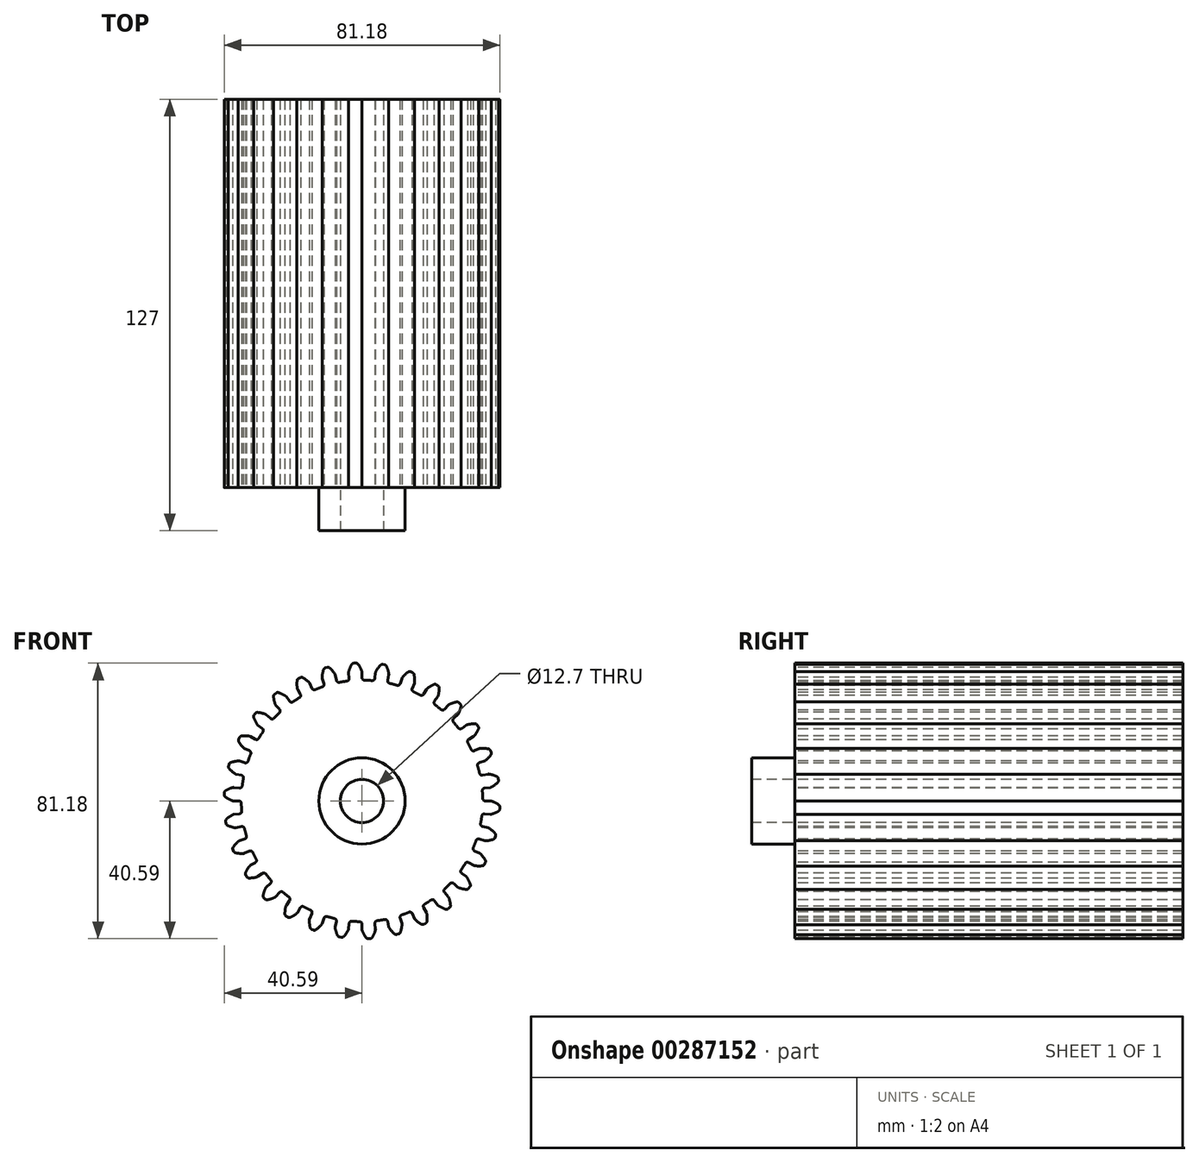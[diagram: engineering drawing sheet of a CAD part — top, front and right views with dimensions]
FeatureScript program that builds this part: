
annotation { "Feature Type Name" : "Feature", "Feature Type Description" : "" }
export const myFeature = defineFeature(function(context is Context, id is Id, definition is map)
    precondition{}
    {
        {
            var Q0;
            Q0=qCreatedBy(makeId("Front.planeOp"),FACE);
            var sketch = newSketch(context, id + "F0", { "sketchPlane" : qUnion([Q0])});
            skCircle(sketch, "E0", {"center": v(0, 0) * mm, "radius": 35.56 * mm});
            skSolve(sketch);
        }
        {
            var Q0;
            Q0=qSketchRegion(id+"F0",true);
            extrude(context, id + "F1", {"entities" : qUnion([Q0]), "depth" : 57.15 * mm});
        }
        {
            var Q0;
            Q0=makeQuery(id+"F1.opExtrude","CAP_FACE",FACE,{"disambiguationData":[OSD([sQuery(id+"F0.wireOp",EDGE,"E0")])],"isStart":true});
            extrude(context, id + "F2", {"entities" : qUnion([Q0]), "operationType" : NewBodyOperationType.ADD, "depth" : 57.15 * mm});
        }
        {
            var Q0;
            Q0=makeQuery(id+"F1.opExtrude","CAP_FACE",FACE,{"disambiguationData":[OSD([sQuery(id+"F0.wireOp",EDGE,"E0")])],"isStart":false});
            var sketch = newSketch(context, id + "F3", { "sketchPlane" : qUnion([Q0])});
            skArc(sketch, "E1.trimOffspring", {"start": v(-0.06, 38.24) * mm, "mid": v(-0.56, 39.3) * mm, "end": v(-1.18, 40.28) * mm});
            skLineSegment(sketch, "E2", {"start": v(-1.84, 40.6) * mm, "end": v(-2.13, 40.58) * mm});
            skLineSegment(sketch, "E3", {"start": v(0, 37.96) * mm, "end": v(0, 36.31) * mm});
            skLineSegment(sketch, "E4.MirrorCS", {"start": v(-2.41, 40.56) * mm, "end": v(-2.13, 40.58) * mm});
            skArc(sketch, "E5.MirrorCS", {"start": v(-3.94, 38.04) * mm, "mid": v(-3.55, 39.14) * mm, "end": v(-3.03, 40.18) * mm});
            skPoint(sketch, "E6.visualSharp", {"position": v(-3.76, 35.36) * mm});
            skPoint(sketch, "E7.visualSharp", {"position": v(0, 35.56) * mm});
            skArc(sketch, "E7.filletArc", {"start": v(0, 36.31) * mm, "mid": v(0.22, 35.78) * mm, "end": v(0.75, 35.55) * mm});
            skArc(sketch, "E8", {"start": v(0.75, 35.55) * mm, "mid": v(-1.88, 35.51) * mm, "end": v(-4.5, 35.27) * mm});
            skLineSegment(sketch, "E9.MirrorCS", {"start": v(-3.97, 37.75) * mm, "end": v(-3.8, 36.12) * mm});
            skArc(sketch, "E10.MirrorCS", {"start": v(-3.8, 36.12) * mm, "mid": v(-3.96, 35.56) * mm, "end": v(-4.46, 35.28) * mm});
            skPoint(sketch, "E11.visualSharp", {"position": v(-3.98, 37.9) * mm});
            skArc(sketch, "E11.filletArc", {"start": v(-3.94, 38.04) * mm, "mid": v(-3.97, 37.9) * mm, "end": v(-3.97, 37.75) * mm});
            skPoint(sketch, "E12.visualSharp", {"position": v(-2.81, 40.54) * mm});
            skArc(sketch, "E12.filletArc", {"start": v(-2.41, 40.56) * mm, "mid": v(-2.77, 40.45) * mm, "end": v(-3.03, 40.18) * mm});
            skPoint(sketch, "E13.visualSharp", {"position": v(-1.44, 40.61) * mm});
            skArc(sketch, "E13.filletArc", {"start": v(-1.18, 40.28) * mm, "mid": v(-1.47, 40.52) * mm, "end": v(-1.84, 40.6) * mm});
            skPoint(sketch, "E14.visualSharp", {"position": v(0, 38.1) * mm});
            skArc(sketch, "E14.filletArc", {"start": v(0, 37.96) * mm, "mid": v(-0.01, 38.1) * mm, "end": v(-0.06, 38.24) * mm});
            skPoint(sketch, "E15.1.0", {"position": v(-11.77, 36.24) * mm});
            skArc(sketch, "E15.1.1", {"start": v(-6.66, 34.93) * mm, "mid": v(-9.22, 34.34) * mm, "end": v(-11.73, 33.57) * mm});
            skLineSegment(sketch, "E15.1.2", {"start": v(-11.73, 36.1) * mm, "end": v(-11.22, 34.54) * mm});
            skArc(sketch, "E15.1.3", {"start": v(-7.55, 35.52) * mm, "mid": v(-7.23, 35.04) * mm, "end": v(-6.66, 34.93) * mm});
            skPoint(sketch, "E15.1.4", {"position": v(-7.92, 37.27) * mm});
            skPoint(sketch, "E15.1.5", {"position": v(-7.4, 34.78) * mm});
            skArc(sketch, "E15.1.6", {"start": v(-11.22, 34.54) * mm, "mid": v(-11.26, 33.96) * mm, "end": v(-11.7, 33.58) * mm});
            skArc(sketch, "E15.1.7", {"start": v(-11.76, 36.39) * mm, "mid": v(-11.61, 37.54) * mm, "end": v(-11.32, 38.68) * mm});
            skPoint(sketch, "E15.1.8", {"position": v(-11.18, 39.07) * mm});
            skArc(sketch, "E15.1.9", {"start": v(-8, 37.4) * mm, "mid": v(-8.72, 38.32) * mm, "end": v(-9.53, 39.15) * mm});
            skPoint(sketch, "E15.1.10", {"position": v(-9.85, 39.43) * mm});
            skPoint(sketch, "E15.1.11", {"position": v(-11.03, 33.8) * mm});
            skLineSegment(sketch, "E15.1.12", {"start": v(-7.9, 37.13) * mm, "end": v(-7.55, 35.52) * mm});
            skArc(sketch, "E15.1.13", {"start": v(-9.53, 39.15) * mm, "mid": v(-9.87, 39.33) * mm, "end": v(-10.24, 39.32) * mm});
            skArc(sketch, "E15.1.14", {"start": v(-10.8, 39.18) * mm, "mid": v(-11.12, 39) * mm, "end": v(-11.32, 38.68) * mm});
            skLineSegment(sketch, "E15.1.15", {"start": v(-10.8, 39.18) * mm, "end": v(-10.52, 39.25) * mm});
            skLineSegment(sketch, "E15.1.16", {"start": v(-10.24, 39.32) * mm, "end": v(-10.52, 39.25) * mm});
            skArc(sketch, "E15.1.17", {"start": v(-11.76, 36.39) * mm, "mid": v(-11.76, 36.24) * mm, "end": v(-11.73, 36.1) * mm});
            skArc(sketch, "E15.1.18", {"start": v(-7.9, 37.13) * mm, "mid": v(-7.94, 37.27) * mm, "end": v(-8, 37.4) * mm});
            skPoint(sketch, "E15.2.0", {"position": v(-19.05, 33) * mm});
            skArc(sketch, "E15.2.1", {"start": v(-13.78, 32.78) * mm, "mid": v(-16.16, 31.67) * mm, "end": v(-18.46, 30.4) * mm});
            skLineSegment(sketch, "E15.2.2", {"start": v(-18.98, 32.87) * mm, "end": v(-18.16, 31.45) * mm});
            skArc(sketch, "E15.2.3", {"start": v(-14.77, 33.17) * mm, "mid": v(-14.35, 32.78) * mm, "end": v(-13.78, 32.78) * mm});
            skPoint(sketch, "E15.2.4", {"position": v(-15.5, 34.8) * mm});
            skPoint(sketch, "E15.2.5", {"position": v(-14.46, 32.49) * mm});
            skArc(sketch, "E15.2.6", {"start": v(-18.16, 31.45) * mm, "mid": v(-18.08, 30.88) * mm, "end": v(-18.42, 30.42) * mm});
            skArc(sketch, "E15.2.7", {"start": v(-19.07, 33.14) * mm, "mid": v(-19.16, 34.3) * mm, "end": v(-19.11, 35.48) * mm});
            skPoint(sketch, "E15.2.8", {"position": v(-19.06, 35.9) * mm});
            skArc(sketch, "E15.2.9", {"start": v(-15.6, 34.91) * mm, "mid": v(-16.5, 35.67) * mm, "end": v(-17.47, 36.32) * mm});
            skPoint(sketch, "E15.2.10", {"position": v(-17.83, 36.52) * mm});
            skPoint(sketch, "E15.2.11", {"position": v(-17.82, 30.77) * mm});
            skLineSegment(sketch, "E15.2.12", {"start": v(-15.44, 34.67) * mm, "end": v(-14.77, 33.17) * mm});
            skArc(sketch, "E15.2.13", {"start": v(-17.47, 36.32) * mm, "mid": v(-17.83, 36.42) * mm, "end": v(-18.2, 36.34) * mm});
            skArc(sketch, "E15.2.14", {"start": v(-18.7, 36.08) * mm, "mid": v(-18.98, 35.83) * mm, "end": v(-19.11, 35.48) * mm});
            skLineSegment(sketch, "E15.2.15", {"start": v(-18.7, 36.08) * mm, "end": v(-18.45, 36.2) * mm});
            skLineSegment(sketch, "E15.2.16", {"start": v(-18.2, 36.34) * mm, "end": v(-18.45, 36.2) * mm});
            skArc(sketch, "E15.2.17", {"start": v(-19.07, 33.14) * mm, "mid": v(-19.04, 33) * mm, "end": v(-18.98, 32.87) * mm});
            skArc(sketch, "E15.2.18", {"start": v(-15.44, 34.67) * mm, "mid": v(-15.5, 34.8) * mm, "end": v(-15.6, 34.91) * mm});
            skArc(sketch, "E16.1.3.0", {"start": v(-20.3, 29.2) * mm, "mid": v(-22.4, 27.62) * mm, "end": v(-24.37, 25.9) * mm});
            skLineSegment(sketch, "E16.5.3.0", {"start": v(-25.4, 28.2) * mm, "end": v(-24.3, 26.99) * mm});
            skArc(sketch, "E16.8.3.0", {"start": v(-21.34, 29.38) * mm, "mid": v(-20.86, 29.08) * mm, "end": v(-20.3, 29.2) * mm});
            skPoint(sketch, "E16.12.3.0", {"position": v(-22.4, 30.82) * mm});
            skPoint(sketch, "E16.13.3.0", {"position": v(-20.9, 28.77) * mm});
            skArc(sketch, "E16.14.3.0", {"start": v(-24.3, 26.99) * mm, "mid": v(-24.1, 26.44) * mm, "end": v(-24.34, 25.92) * mm});
            skArc(sketch, "E16.18.3.0", {"start": v(-25.55, 28.45) * mm, "mid": v(-25.88, 29.57) * mm, "end": v(-26.07, 30.73) * mm});
            skPoint(sketch, "E16.22.3.0", {"position": v(-26.1, 31.15) * mm});
            skArc(sketch, "E16.23.3.0", {"start": v(-22.52, 30.9) * mm, "mid": v(-23.55, 31.46) * mm, "end": v(-24.63, 31.9) * mm});
            skPoint(sketch, "E16.24.3.0", {"position": v(-25.5, 28.31) * mm});
            skPoint(sketch, "E16.27.3.0", {"position": v(-25.04, 32.01) * mm});
            skPoint(sketch, "E16.28.3.0", {"position": v(-23.83, 26.4) * mm});
            skLineSegment(sketch, "E16.29.3.0", {"start": v(-22.3, 30.7) * mm, "end": v(-21.34, 29.38) * mm});
            skArc(sketch, "E16.32.3.0", {"start": v(-24.63, 31.9) * mm, "mid": v(-25, 31.92) * mm, "end": v(-25.35, 31.76) * mm});
            skArc(sketch, "E16.36.3.0", {"start": v(-25.8, 31.4) * mm, "mid": v(-26.02, 31.1) * mm, "end": v(-26.07, 30.73) * mm});
            skLineSegment(sketch, "E16.40.3.0", {"start": v(-25.8, 31.4) * mm, "end": v(-25.57, 31.58) * mm});
            skLineSegment(sketch, "E16.43.3.0", {"start": v(-25.35, 31.76) * mm, "end": v(-25.57, 31.58) * mm});
            skArc(sketch, "E16.46.3.0", {"start": v(-25.55, 28.45) * mm, "mid": v(-25.48, 28.32) * mm, "end": v(-25.4, 28.2) * mm});
            skArc(sketch, "E16.50.3.0", {"start": v(-22.3, 30.7) * mm, "mid": v(-22.4, 30.82) * mm, "end": v(-22.52, 30.9) * mm});
            skArc(sketch, "E16.1.4.0", {"start": v(-25.92, 24.34) * mm, "mid": v(-27.65, 22.36) * mm, "end": v(-29.22, 20.26) * mm});
            skLineSegment(sketch, "E16.5.4.0", {"start": v(-30.7, 22.3) * mm, "end": v(-29.38, 21.34) * mm});
            skArc(sketch, "E16.8.4.0", {"start": v(-26.99, 24.3) * mm, "mid": v(-26.44, 24.1) * mm, "end": v(-25.92, 24.34) * mm});
            skPoint(sketch, "E16.12.4.0", {"position": v(-28.31, 25.5) * mm});
            skPoint(sketch, "E16.13.4.0", {"position": v(-26.43, 23.8) * mm});
            skArc(sketch, "E16.14.4.0", {"start": v(-29.38, 21.34) * mm, "mid": v(-29.08, 20.86) * mm, "end": v(-29.2, 20.3) * mm});
            skArc(sketch, "E16.18.4.0", {"start": v(-30.9, 22.52) * mm, "mid": v(-31.46, 23.55) * mm, "end": v(-31.9, 24.63) * mm});
            skPoint(sketch, "E16.22.4.0", {"position": v(-32.01, 25.04) * mm});
            skArc(sketch, "E16.23.4.0", {"start": v(-28.45, 25.55) * mm, "mid": v(-29.57, 25.88) * mm, "end": v(-30.73, 26.07) * mm});
            skPoint(sketch, "E16.24.4.0", {"position": v(-30.82, 22.4) * mm});
            skPoint(sketch, "E16.27.4.0", {"position": v(-31.15, 26.1) * mm});
            skPoint(sketch, "E16.28.4.0", {"position": v(-28.8, 20.87) * mm});
            skLineSegment(sketch, "E16.29.4.0", {"start": v(-28.2, 25.4) * mm, "end": v(-26.99, 24.3) * mm});
            skArc(sketch, "E16.32.4.0", {"start": v(-30.73, 26.07) * mm, "mid": v(-31.1, 26.02) * mm, "end": v(-31.4, 25.8) * mm});
            skArc(sketch, "E16.36.4.0", {"start": v(-31.76, 25.35) * mm, "mid": v(-31.92, 25) * mm, "end": v(-31.9, 24.63) * mm});
            skLineSegment(sketch, "E16.40.4.0", {"start": v(-31.76, 25.35) * mm, "end": v(-31.58, 25.57) * mm});
            skLineSegment(sketch, "E16.43.4.0", {"start": v(-31.4, 25.8) * mm, "end": v(-31.58, 25.57) * mm});
            skArc(sketch, "E16.46.4.0", {"start": v(-30.9, 22.52) * mm, "mid": v(-30.82, 22.4) * mm, "end": v(-30.7, 22.3) * mm});
            skArc(sketch, "E16.50.4.0", {"start": v(-28.2, 25.4) * mm, "mid": v(-28.32, 25.48) * mm, "end": v(-28.45, 25.55) * mm});
            skArc(sketch, "E16.1.5.0", {"start": v(-30.42, 18.42) * mm, "mid": v(-31.7, 16.13) * mm, "end": v(-32.8, 13.74) * mm});
            skLineSegment(sketch, "E16.5.5.0", {"start": v(-34.67, 15.44) * mm, "end": v(-33.17, 14.77) * mm});
            skArc(sketch, "E16.8.5.0", {"start": v(-31.45, 18.16) * mm, "mid": v(-30.88, 18.08) * mm, "end": v(-30.42, 18.42) * mm});
            skPoint(sketch, "E16.12.5.0", {"position": v(-33, 19.05) * mm});
            skPoint(sketch, "E16.13.5.0", {"position": v(-30.8, 17.78) * mm});
            skArc(sketch, "E16.14.5.0", {"start": v(-33.17, 14.77) * mm, "mid": v(-32.78, 14.35) * mm, "end": v(-32.78, 13.78) * mm});
            skArc(sketch, "E16.18.5.0", {"start": v(-34.91, 15.6) * mm, "mid": v(-35.67, 16.5) * mm, "end": v(-36.32, 17.47) * mm});
            skPoint(sketch, "E16.22.5.0", {"position": v(-36.52, 17.83) * mm});
            skArc(sketch, "E16.23.5.0", {"start": v(-33.14, 19.07) * mm, "mid": v(-34.3, 19.16) * mm, "end": v(-35.48, 19.11) * mm});
            skPoint(sketch, "E16.24.5.0", {"position": v(-34.8, 15.5) * mm});
            skPoint(sketch, "E16.27.5.0", {"position": v(-35.9, 19.06) * mm});
            skPoint(sketch, "E16.28.5.0", {"position": v(-32.5, 14.42) * mm});
            skLineSegment(sketch, "E16.29.5.0", {"start": v(-32.87, 18.98) * mm, "end": v(-31.45, 18.16) * mm});
            skArc(sketch, "E16.32.5.0", {"start": v(-35.48, 19.11) * mm, "mid": v(-35.83, 18.98) * mm, "end": v(-36.08, 18.7) * mm});
            skArc(sketch, "E16.36.5.0", {"start": v(-36.34, 18.2) * mm, "mid": v(-36.42, 17.83) * mm, "end": v(-36.32, 17.47) * mm});
            skLineSegment(sketch, "E16.40.5.0", {"start": v(-36.34, 18.2) * mm, "end": v(-36.2, 18.45) * mm});
            skLineSegment(sketch, "E16.43.5.0", {"start": v(-36.08, 18.7) * mm, "end": v(-36.2, 18.45) * mm});
            skArc(sketch, "E16.46.5.0", {"start": v(-34.91, 15.6) * mm, "mid": v(-34.8, 15.5) * mm, "end": v(-34.67, 15.44) * mm});
            skArc(sketch, "E16.50.5.0", {"start": v(-32.87, 18.98) * mm, "mid": v(-33, 19.04) * mm, "end": v(-33.14, 19.07) * mm});
            skArc(sketch, "E16.1.6.0", {"start": v(-33.58, 11.7) * mm, "mid": v(-34.35, 9.18) * mm, "end": v(-34.94, 6.62) * mm});
            skLineSegment(sketch, "E16.5.6.0", {"start": v(-37.13, 7.9) * mm, "end": v(-35.52, 7.55) * mm});
            skArc(sketch, "E16.8.6.0", {"start": v(-34.54, 11.22) * mm, "mid": v(-33.96, 11.26) * mm, "end": v(-33.58, 11.7) * mm});
            skPoint(sketch, "E16.12.6.0", {"position": v(-36.24, 11.77) * mm});
            skPoint(sketch, "E16.13.6.0", {"position": v(-33.82, 10.99) * mm});
            skArc(sketch, "E16.14.6.0", {"start": v(-35.52, 7.55) * mm, "mid": v(-35.04, 7.23) * mm, "end": v(-34.93, 6.66) * mm});
            skArc(sketch, "E16.18.6.0", {"start": v(-37.4, 8) * mm, "mid": v(-38.32, 8.72) * mm, "end": v(-39.15, 9.53) * mm});
            skPoint(sketch, "E16.22.6.0", {"position": v(-39.43, 9.85) * mm});
            skArc(sketch, "E16.23.6.0", {"start": v(-36.39, 11.76) * mm, "mid": v(-37.54, 11.61) * mm, "end": v(-38.68, 11.32) * mm});
            skPoint(sketch, "E16.24.6.0", {"position": v(-37.27, 7.92) * mm});
            skPoint(sketch, "E16.27.6.0", {"position": v(-39.07, 11.18) * mm});
            skPoint(sketch, "E16.28.6.0", {"position": v(-34.8, 7.35) * mm});
            skLineSegment(sketch, "E16.29.6.0", {"start": v(-36.1, 11.73) * mm, "end": v(-34.54, 11.22) * mm});
            skArc(sketch, "E16.32.6.0", {"start": v(-38.68, 11.32) * mm, "mid": v(-39, 11.12) * mm, "end": v(-39.18, 10.8) * mm});
            skArc(sketch, "E16.36.6.0", {"start": v(-39.32, 10.24) * mm, "mid": v(-39.33, 9.87) * mm, "end": v(-39.15, 9.53) * mm});
            skLineSegment(sketch, "E16.40.6.0", {"start": v(-39.32, 10.24) * mm, "end": v(-39.25, 10.52) * mm});
            skLineSegment(sketch, "E16.43.6.0", {"start": v(-39.18, 10.8) * mm, "end": v(-39.25, 10.52) * mm});
            skArc(sketch, "E16.46.6.0", {"start": v(-37.4, 8) * mm, "mid": v(-37.27, 7.94) * mm, "end": v(-37.13, 7.9) * mm});
            skArc(sketch, "E16.50.6.0", {"start": v(-36.1, 11.73) * mm, "mid": v(-36.24, 11.76) * mm, "end": v(-36.39, 11.76) * mm});
            skArc(sketch, "E16.1.7.0", {"start": v(-35.28, 4.46) * mm, "mid": v(-35.51, 1.84) * mm, "end": v(-35.55, -0.79) * mm});
            skLineSegment(sketch, "E16.5.7.0", {"start": v(-37.96, 0) * mm, "end": v(-36.31, 0) * mm});
            skArc(sketch, "E16.8.7.0", {"start": v(-36.12, 3.8) * mm, "mid": v(-35.56, 3.96) * mm, "end": v(-35.28, 4.46) * mm});
            skPoint(sketch, "E16.12.7.0", {"position": v(-37.9, 3.98) * mm});
            skPoint(sketch, "E16.13.7.0", {"position": v(-35.37, 3.72) * mm});
            skArc(sketch, "E16.14.7.0", {"start": v(-36.31, 0) * mm, "mid": v(-35.78, -0.22) * mm, "end": v(-35.55, -0.75) * mm});
            skArc(sketch, "E16.18.7.0", {"start": v(-38.24, 0.06) * mm, "mid": v(-39.3, 0.56) * mm, "end": v(-40.28, 1.18) * mm});
            skPoint(sketch, "E16.22.7.0", {"position": v(-40.61, 1.44) * mm});
            skArc(sketch, "E16.23.7.0", {"start": v(-38.04, 3.94) * mm, "mid": v(-39.14, 3.55) * mm, "end": v(-40.18, 3.03) * mm});
            skPoint(sketch, "E16.24.7.0", {"position": v(-38.1, 0) * mm});
            skPoint(sketch, "E16.27.7.0", {"position": v(-40.54, 2.81) * mm});
            skPoint(sketch, "E16.28.7.0", {"position": v(-35.56, -0.04) * mm});
            skLineSegment(sketch, "E16.29.7.0", {"start": v(-37.75, 3.97) * mm, "end": v(-36.12, 3.8) * mm});
            skArc(sketch, "E16.32.7.0", {"start": v(-40.18, 3.03) * mm, "mid": v(-40.45, 2.77) * mm, "end": v(-40.56, 2.41) * mm});
            skArc(sketch, "E16.36.7.0", {"start": v(-40.6, 1.84) * mm, "mid": v(-40.52, 1.47) * mm, "end": v(-40.28, 1.18) * mm});
            skLineSegment(sketch, "E16.40.7.0", {"start": v(-40.6, 1.84) * mm, "end": v(-40.58, 2.13) * mm});
            skLineSegment(sketch, "E16.43.7.0", {"start": v(-40.56, 2.41) * mm, "end": v(-40.58, 2.13) * mm});
            skArc(sketch, "E16.46.7.0", {"start": v(-38.24, 0.06) * mm, "mid": v(-38.1, 0.01) * mm, "end": v(-37.96, 0) * mm});
            skArc(sketch, "E16.50.7.0", {"start": v(-37.75, 3.97) * mm, "mid": v(-37.9, 3.97) * mm, "end": v(-38.04, 3.94) * mm});
            skArc(sketch, "E16.1.8.0", {"start": v(-35.44, -2.97) * mm, "mid": v(-35.12, -5.58) * mm, "end": v(-34.61, -8.16) * mm});
            skLineSegment(sketch, "E16.5.8.0", {"start": v(-37.13, -7.9) * mm, "end": v(-35.52, -7.55) * mm});
            skArc(sketch, "E16.8.8.0", {"start": v(-36.12, -3.8) * mm, "mid": v(-35.6, -3.52) * mm, "end": v(-35.44, -2.97) * mm});
            skPoint(sketch, "E16.12.8.0", {"position": v(-37.9, -3.98) * mm});
            skPoint(sketch, "E16.13.8.0", {"position": v(-35.37, -3.72) * mm});
            skArc(sketch, "E16.14.8.0", {"start": v(-35.52, -7.55) * mm, "mid": v(-34.95, -7.65) * mm, "end": v(-34.62, -8.12) * mm});
            skArc(sketch, "E16.18.8.0", {"start": v(-37.42, -7.9) * mm, "mid": v(-38.55, -7.62) * mm, "end": v(-39.65, -7.22) * mm});
            skPoint(sketch, "E16.22.8.0", {"position": v(-40.03, -7.04) * mm});
            skArc(sketch, "E16.23.8.0", {"start": v(-38.02, -4.05) * mm, "mid": v(-39.02, -4.66) * mm, "end": v(-39.94, -5.39) * mm});
            skPoint(sketch, "E16.24.8.0", {"position": v(-37.27, -7.92) * mm});
            skPoint(sketch, "E16.27.8.0", {"position": v(-40.24, -5.68) * mm});
            skPoint(sketch, "E16.28.8.0", {"position": v(-34.77, -7.43) * mm});
            skLineSegment(sketch, "E16.29.8.0", {"start": v(-37.75, -3.97) * mm, "end": v(-36.12, -3.8) * mm});
            skArc(sketch, "E16.32.8.0", {"start": v(-39.94, -5.39) * mm, "mid": v(-40.14, -5.7) * mm, "end": v(-40.18, -6.07) * mm});
            skArc(sketch, "E16.36.8.0", {"start": v(-40.09, -6.64) * mm, "mid": v(-39.94, -6.98) * mm, "end": v(-39.65, -7.22) * mm});
            skLineSegment(sketch, "E16.40.8.0", {"start": v(-40.09, -6.64) * mm, "end": v(-40.13, -6.36) * mm});
            skLineSegment(sketch, "E16.43.8.0", {"start": v(-40.18, -6.07) * mm, "end": v(-40.13, -6.36) * mm});
            skArc(sketch, "E16.46.8.0", {"start": v(-37.42, -7.9) * mm, "mid": v(-37.27, -7.9) * mm, "end": v(-37.13, -7.9) * mm});
            skArc(sketch, "E16.50.8.0", {"start": v(-37.75, -3.97) * mm, "mid": v(-37.9, -4) * mm, "end": v(-38.02, -4.05) * mm});
            skArc(sketch, "E16.1.9.0", {"start": v(-34.04, -10.28) * mm, "mid": v(-33.2, -12.76) * mm, "end": v(-32.16, -15.18) * mm});
            skLineSegment(sketch, "E16.5.9.0", {"start": v(-34.67, -15.44) * mm, "end": v(-33.17, -14.77) * mm});
            skArc(sketch, "E16.8.9.0", {"start": v(-34.54, -11.22) * mm, "mid": v(-34.1, -10.85) * mm, "end": v(-34.04, -10.28) * mm});
            skPoint(sketch, "E16.12.9.0", {"position": v(-36.24, -11.77) * mm});
            skPoint(sketch, "E16.13.9.0", {"position": v(-33.82, -10.99) * mm});
            skArc(sketch, "E16.14.9.0", {"start": v(-33.17, -14.77) * mm, "mid": v(-32.6, -14.75) * mm, "end": v(-32.18, -15.14) * mm});
            skArc(sketch, "E16.18.9.0", {"start": v(-34.96, -15.5) * mm, "mid": v(-36.12, -15.47) * mm, "end": v(-37.28, -15.3) * mm});
            skPoint(sketch, "E16.22.9.0", {"position": v(-37.69, -15.2) * mm});
            skArc(sketch, "E16.23.9.0", {"start": v(-36.35, -11.87) * mm, "mid": v(-37.2, -12.67) * mm, "end": v(-37.94, -13.57) * mm});
            skPoint(sketch, "E16.24.9.0", {"position": v(-34.8, -15.5) * mm});
            skPoint(sketch, "E16.27.9.0", {"position": v(-38.18, -13.92) * mm});
            skPoint(sketch, "E16.28.9.0", {"position": v(-32.47, -14.5) * mm});
            skLineSegment(sketch, "E16.29.9.0", {"start": v(-36.1, -11.73) * mm, "end": v(-34.54, -11.22) * mm});
            skArc(sketch, "E16.32.9.0", {"start": v(-37.94, -13.57) * mm, "mid": v(-38.08, -13.92) * mm, "end": v(-38.04, -14.3) * mm});
            skArc(sketch, "E16.36.9.0", {"start": v(-37.83, -14.83) * mm, "mid": v(-37.62, -15.14) * mm, "end": v(-37.28, -15.3) * mm});
            skLineSegment(sketch, "E16.40.9.0", {"start": v(-37.83, -14.83) * mm, "end": v(-37.94, -14.56) * mm});
            skLineSegment(sketch, "E16.43.9.0", {"start": v(-38.04, -14.3) * mm, "end": v(-37.94, -14.56) * mm});
            skArc(sketch, "E16.46.9.0", {"start": v(-34.96, -15.5) * mm, "mid": v(-34.81, -15.48) * mm, "end": v(-34.67, -15.44) * mm});
            skArc(sketch, "E16.50.9.0", {"start": v(-36.1, -11.73) * mm, "mid": v(-36.23, -11.79) * mm, "end": v(-36.35, -11.87) * mm});
            skArc(sketch, "E16.1.10.0", {"start": v(-31.16, -17.13) * mm, "mid": v(-29.81, -19.38) * mm, "end": v(-28.3, -21.53) * mm});
            skLineSegment(sketch, "E16.5.10.0", {"start": v(-30.7, -22.3) * mm, "end": v(-29.38, -21.34) * mm});
            skArc(sketch, "E16.8.10.0", {"start": v(-31.45, -18.16) * mm, "mid": v(-31.1, -17.7) * mm, "end": v(-31.16, -17.13) * mm});
            skPoint(sketch, "E16.12.10.0", {"position": v(-33, -19.05) * mm});
            skPoint(sketch, "E16.13.10.0", {"position": v(-30.8, -17.78) * mm});
            skArc(sketch, "E16.14.10.0", {"start": v(-29.38, -21.34) * mm, "mid": v(-28.82, -21.2) * mm, "end": v(-28.32, -21.5) * mm});
            skArc(sketch, "E16.18.10.0", {"start": v(-30.97, -22.43) * mm, "mid": v(-32.12, -22.65) * mm, "end": v(-33.28, -22.72) * mm});
            skPoint(sketch, "E16.22.10.0", {"position": v(-33.7, -22.7) * mm});
            skArc(sketch, "E16.23.10.0", {"start": v(-33.09, -19.17) * mm, "mid": v(-33.75, -20.13) * mm, "end": v(-34.3, -21.17) * mm});
            skPoint(sketch, "E16.24.10.0", {"position": v(-30.82, -22.4) * mm});
            skPoint(sketch, "E16.27.10.0", {"position": v(-34.45, -21.55) * mm});
            skPoint(sketch, "E16.28.10.0", {"position": v(-28.74, -20.94) * mm});
            skLineSegment(sketch, "E16.29.10.0", {"start": v(-32.87, -18.98) * mm, "end": v(-31.45, -18.16) * mm});
            skArc(sketch, "E16.32.10.0", {"start": v(-34.3, -21.17) * mm, "mid": v(-34.35, -21.54) * mm, "end": v(-34.23, -21.9) * mm});
            skArc(sketch, "E16.36.10.0", {"start": v(-33.92, -22.37) * mm, "mid": v(-33.65, -22.63) * mm, "end": v(-33.28, -22.72) * mm});
            skLineSegment(sketch, "E16.40.10.0", {"start": v(-33.92, -22.37) * mm, "end": v(-34.08, -22.13) * mm});
            skLineSegment(sketch, "E16.43.10.0", {"start": v(-34.23, -21.9) * mm, "end": v(-34.08, -22.13) * mm});
            skArc(sketch, "E16.46.10.0", {"start": v(-30.97, -22.43) * mm, "mid": v(-30.83, -22.38) * mm, "end": v(-30.7, -22.3) * mm});
            skArc(sketch, "E16.50.10.0", {"start": v(-32.87, -18.98) * mm, "mid": v(-32.99, -19.06) * mm, "end": v(-33.09, -19.17) * mm});
            skArc(sketch, "E16.1.11.0", {"start": v(-26.92, -23.23) * mm, "mid": v(-25.13, -25.16) * mm, "end": v(-23.2, -26.95) * mm});
            skLineSegment(sketch, "E16.5.11.0", {"start": v(-25.4, -28.2) * mm, "end": v(-24.3, -26.99) * mm});
            skArc(sketch, "E16.8.11.0", {"start": v(-26.99, -24.3) * mm, "mid": v(-26.74, -23.78) * mm, "end": v(-26.92, -23.23) * mm});
            skPoint(sketch, "E16.12.11.0", {"position": v(-28.31, -25.5) * mm});
            skPoint(sketch, "E16.13.11.0", {"position": v(-26.43, -23.8) * mm});
            skArc(sketch, "E16.14.11.0", {"start": v(-24.3, -26.99) * mm, "mid": v(-23.78, -26.74) * mm, "end": v(-23.23, -26.92) * mm});
            skArc(sketch, "E16.18.11.0", {"start": v(-25.63, -28.38) * mm, "mid": v(-26.7, -28.83) * mm, "end": v(-27.83, -29.14) * mm});
            skPoint(sketch, "E16.22.11.0", {"position": v(-28.25, -29.22) * mm});
            skArc(sketch, "E16.23.11.0", {"start": v(-28.38, -25.63) * mm, "mid": v(-28.83, -26.7) * mm, "end": v(-29.14, -27.83) * mm});
            skPoint(sketch, "E16.24.11.0", {"position": v(-25.5, -28.31) * mm});
            skPoint(sketch, "E16.27.11.0", {"position": v(-29.22, -28.25) * mm});
            skPoint(sketch, "E16.28.11.0", {"position": v(-23.76, -26.45) * mm});
            skLineSegment(sketch, "E16.29.11.0", {"start": v(-28.2, -25.4) * mm, "end": v(-26.99, -24.3) * mm});
            skArc(sketch, "E16.32.11.0", {"start": v(-29.14, -27.83) * mm, "mid": v(-29.13, -28.2) * mm, "end": v(-28.93, -28.53) * mm});
            skArc(sketch, "E16.36.11.0", {"start": v(-28.53, -28.93) * mm, "mid": v(-28.2, -29.13) * mm, "end": v(-27.83, -29.14) * mm});
            skLineSegment(sketch, "E16.40.11.0", {"start": v(-28.53, -28.93) * mm, "end": v(-28.73, -28.73) * mm});
            skLineSegment(sketch, "E16.43.11.0", {"start": v(-28.93, -28.53) * mm, "end": v(-28.73, -28.73) * mm});
            skArc(sketch, "E16.46.11.0", {"start": v(-25.63, -28.38) * mm, "mid": v(-25.5, -28.3) * mm, "end": v(-25.4, -28.2) * mm});
            skArc(sketch, "E16.50.11.0", {"start": v(-28.2, -25.4) * mm, "mid": v(-28.3, -25.5) * mm, "end": v(-28.38, -25.63) * mm});
            skArc(sketch, "E16.1.12.0", {"start": v(-21.5, -28.32) * mm, "mid": v(-19.35, -29.83) * mm, "end": v(-17.1, -31.18) * mm});
            skLineSegment(sketch, "E16.5.12.0", {"start": v(-18.98, -32.87) * mm, "end": v(-18.16, -31.45) * mm});
            skArc(sketch, "E16.8.12.0", {"start": v(-21.34, -29.38) * mm, "mid": v(-21.2, -28.82) * mm, "end": v(-21.5, -28.32) * mm});
            skPoint(sketch, "E16.12.12.0", {"position": v(-22.4, -30.82) * mm});
            skPoint(sketch, "E16.13.12.0", {"position": v(-20.9, -28.77) * mm});
            skArc(sketch, "E16.14.12.0", {"start": v(-18.16, -31.45) * mm, "mid": v(-17.7, -31.1) * mm, "end": v(-17.13, -31.16) * mm});
            skArc(sketch, "E16.18.12.0", {"start": v(-19.17, -33.09) * mm, "mid": v(-20.13, -33.75) * mm, "end": v(-21.17, -34.3) * mm});
            skPoint(sketch, "E16.22.12.0", {"position": v(-21.55, -34.45) * mm});
            skArc(sketch, "E16.23.12.0", {"start": v(-22.43, -30.97) * mm, "mid": v(-22.65, -32.12) * mm, "end": v(-22.72, -33.28) * mm});
            skPoint(sketch, "E16.24.12.0", {"position": v(-19.05, -33) * mm});
            skPoint(sketch, "E16.27.12.0", {"position": v(-22.7, -33.7) * mm});
            skPoint(sketch, "E16.28.12.0", {"position": v(-17.74, -30.82) * mm});
            skLineSegment(sketch, "E16.29.12.0", {"start": v(-22.3, -30.7) * mm, "end": v(-21.34, -29.38) * mm});
            skArc(sketch, "E16.32.12.0", {"start": v(-22.72, -33.28) * mm, "mid": v(-22.63, -33.65) * mm, "end": v(-22.37, -33.92) * mm});
            skArc(sketch, "E16.36.12.0", {"start": v(-21.9, -34.23) * mm, "mid": v(-21.54, -34.35) * mm, "end": v(-21.17, -34.3) * mm});
            skLineSegment(sketch, "E16.40.12.0", {"start": v(-21.9, -34.23) * mm, "end": v(-22.13, -34.08) * mm});
            skLineSegment(sketch, "E16.43.12.0", {"start": v(-22.37, -33.92) * mm, "end": v(-22.13, -34.08) * mm});
            skArc(sketch, "E16.46.12.0", {"start": v(-19.17, -33.09) * mm, "mid": v(-19.06, -32.99) * mm, "end": v(-18.98, -32.87) * mm});
            skArc(sketch, "E16.50.12.0", {"start": v(-22.3, -30.7) * mm, "mid": v(-22.38, -30.83) * mm, "end": v(-22.43, -30.97) * mm});
            skArc(sketch, "E16.1.13.0", {"start": v(-15.14, -32.18) * mm, "mid": v(-12.72, -33.2) * mm, "end": v(-10.24, -34.05) * mm});
            skLineSegment(sketch, "E16.5.13.0", {"start": v(-11.73, -36.1) * mm, "end": v(-11.22, -34.54) * mm});
            skArc(sketch, "E16.8.13.0", {"start": v(-14.77, -33.17) * mm, "mid": v(-14.75, -32.6) * mm, "end": v(-15.14, -32.18) * mm});
            skPoint(sketch, "E16.12.13.0", {"position": v(-15.5, -34.8) * mm});
            skPoint(sketch, "E16.13.13.0", {"position": v(-14.46, -32.49) * mm});
            skArc(sketch, "E16.14.13.0", {"start": v(-11.22, -34.54) * mm, "mid": v(-10.85, -34.1) * mm, "end": v(-10.28, -34.04) * mm});
            skArc(sketch, "E16.18.13.0", {"start": v(-11.87, -36.35) * mm, "mid": v(-12.67, -37.2) * mm, "end": v(-13.57, -37.94) * mm});
            skPoint(sketch, "E16.22.13.0", {"position": v(-13.92, -38.18) * mm});
            skArc(sketch, "E16.23.13.0", {"start": v(-15.5, -34.96) * mm, "mid": v(-15.47, -36.12) * mm, "end": v(-15.3, -37.28) * mm});
            skPoint(sketch, "E16.24.13.0", {"position": v(-11.77, -36.24) * mm});
            skPoint(sketch, "E16.27.13.0", {"position": v(-15.2, -37.69) * mm});
            skPoint(sketch, "E16.28.13.0", {"position": v(-10.95, -33.83) * mm});
            skLineSegment(sketch, "E16.29.13.0", {"start": v(-15.44, -34.67) * mm, "end": v(-14.77, -33.17) * mm});
            skArc(sketch, "E16.32.13.0", {"start": v(-15.3, -37.28) * mm, "mid": v(-15.14, -37.62) * mm, "end": v(-14.83, -37.83) * mm});
            skArc(sketch, "E16.36.13.0", {"start": v(-14.3, -38.04) * mm, "mid": v(-13.92, -38.08) * mm, "end": v(-13.57, -37.94) * mm});
            skLineSegment(sketch, "E16.40.13.0", {"start": v(-14.3, -38.04) * mm, "end": v(-14.56, -37.94) * mm});
            skLineSegment(sketch, "E16.43.13.0", {"start": v(-14.83, -37.83) * mm, "end": v(-14.56, -37.94) * mm});
            skArc(sketch, "E16.46.13.0", {"start": v(-11.87, -36.35) * mm, "mid": v(-11.79, -36.23) * mm, "end": v(-11.73, -36.1) * mm});
            skArc(sketch, "E16.50.13.0", {"start": v(-15.44, -34.67) * mm, "mid": v(-15.48, -34.81) * mm, "end": v(-15.5, -34.96) * mm});
            skArc(sketch, "E16.1.14.0", {"start": v(-8.12, -34.62) * mm, "mid": v(-5.54, -35.13) * mm, "end": v(-2.93, -35.44) * mm});
            skLineSegment(sketch, "E16.5.14.0", {"start": v(-3.97, -37.75) * mm, "end": v(-3.8, -36.12) * mm});
            skArc(sketch, "E16.8.14.0", {"start": v(-7.55, -35.52) * mm, "mid": v(-7.65, -34.95) * mm, "end": v(-8.12, -34.62) * mm});
            skPoint(sketch, "E16.12.14.0", {"position": v(-7.92, -37.27) * mm});
            skPoint(sketch, "E16.13.14.0", {"position": v(-7.4, -34.78) * mm});
            skArc(sketch, "E16.14.14.0", {"start": v(-3.8, -36.12) * mm, "mid": v(-3.52, -35.6) * mm, "end": v(-2.97, -35.44) * mm});
            skArc(sketch, "E16.18.14.0", {"start": v(-4.05, -38.02) * mm, "mid": v(-4.66, -39.02) * mm, "end": v(-5.39, -39.94) * mm});
            skPoint(sketch, "E16.22.14.0", {"position": v(-5.68, -40.24) * mm});
            skArc(sketch, "E16.23.14.0", {"start": v(-7.9, -37.42) * mm, "mid": v(-7.62, -38.55) * mm, "end": v(-7.22, -39.65) * mm});
            skPoint(sketch, "E16.24.14.0", {"position": v(-3.98, -37.9) * mm});
            skPoint(sketch, "E16.27.14.0", {"position": v(-7.04, -40.03) * mm});
            skPoint(sketch, "E16.28.14.0", {"position": v(-3.67, -35.37) * mm});
            skLineSegment(sketch, "E16.29.14.0", {"start": v(-7.9, -37.13) * mm, "end": v(-7.55, -35.52) * mm});
            skArc(sketch, "E16.32.14.0", {"start": v(-7.22, -39.65) * mm, "mid": v(-6.98, -39.94) * mm, "end": v(-6.64, -40.09) * mm});
            skArc(sketch, "E16.36.14.0", {"start": v(-6.07, -40.18) * mm, "mid": v(-5.7, -40.14) * mm, "end": v(-5.39, -39.94) * mm});
            skLineSegment(sketch, "E16.40.14.0", {"start": v(-6.07, -40.18) * mm, "end": v(-6.36, -40.13) * mm});
            skLineSegment(sketch, "E16.43.14.0", {"start": v(-6.64, -40.09) * mm, "end": v(-6.36, -40.13) * mm});
            skArc(sketch, "E16.46.14.0", {"start": v(-4.05, -38.02) * mm, "mid": v(-4, -37.9) * mm, "end": v(-3.97, -37.75) * mm});
            skArc(sketch, "E16.50.14.0", {"start": v(-7.9, -37.13) * mm, "mid": v(-7.9, -37.27) * mm, "end": v(-7.9, -37.42) * mm});
            skArc(sketch, "E16.1.15.0", {"start": v(-0.75, -35.55) * mm, "mid": v(1.88, -35.51) * mm, "end": v(4.5, -35.27) * mm});
            skLineSegment(sketch, "E16.5.15.0", {"start": v(3.97, -37.75) * mm, "end": v(3.8, -36.12) * mm});
            skArc(sketch, "E16.8.15.0", {"start": v(0, -36.31) * mm, "mid": v(-0.22, -35.78) * mm, "end": v(-0.75, -35.55) * mm});
            skPoint(sketch, "E16.12.15.0", {"position": v(0, -38.1) * mm});
            skPoint(sketch, "E16.13.15.0", {"position": v(0, -35.56) * mm});
            skArc(sketch, "E16.14.15.0", {"start": v(3.8, -36.12) * mm, "mid": v(3.96, -35.56) * mm, "end": v(4.46, -35.28) * mm});
            skArc(sketch, "E16.18.15.0", {"start": v(3.94, -38.04) * mm, "mid": v(3.55, -39.14) * mm, "end": v(3.03, -40.18) * mm});
            skPoint(sketch, "E16.22.15.0", {"position": v(2.81, -40.54) * mm});
            skArc(sketch, "E16.23.15.0", {"start": v(0.06, -38.24) * mm, "mid": v(0.56, -39.3) * mm, "end": v(1.18, -40.28) * mm});
            skPoint(sketch, "E16.24.15.0", {"position": v(3.98, -37.9) * mm});
            skPoint(sketch, "E16.27.15.0", {"position": v(1.44, -40.61) * mm});
            skPoint(sketch, "E16.28.15.0", {"position": v(3.76, -35.36) * mm});
            skLineSegment(sketch, "E16.29.15.0", {"start": v(0, -37.96) * mm, "end": v(0, -36.31) * mm});
            skArc(sketch, "E16.32.15.0", {"start": v(1.18, -40.28) * mm, "mid": v(1.47, -40.52) * mm, "end": v(1.84, -40.6) * mm});
            skArc(sketch, "E16.36.15.0", {"start": v(2.41, -40.56) * mm, "mid": v(2.77, -40.45) * mm, "end": v(3.03, -40.18) * mm});
            skLineSegment(sketch, "E16.40.15.0", {"start": v(2.41, -40.56) * mm, "end": v(2.13, -40.58) * mm});
            skLineSegment(sketch, "E16.43.15.0", {"start": v(1.84, -40.6) * mm, "end": v(2.13, -40.58) * mm});
            skArc(sketch, "E16.46.15.0", {"start": v(3.94, -38.04) * mm, "mid": v(3.97, -37.9) * mm, "end": v(3.97, -37.75) * mm});
            skArc(sketch, "E16.50.15.0", {"start": v(0, -37.96) * mm, "mid": v(0.01, -38.1) * mm, "end": v(0.06, -38.24) * mm});
            skArc(sketch, "E16.1.16.0", {"start": v(6.66, -34.93) * mm, "mid": v(9.22, -34.34) * mm, "end": v(11.73, -33.57) * mm});
            skLineSegment(sketch, "E16.5.16.0", {"start": v(11.73, -36.1) * mm, "end": v(11.22, -34.54) * mm});
            skArc(sketch, "E16.8.16.0", {"start": v(7.55, -35.52) * mm, "mid": v(7.23, -35.04) * mm, "end": v(6.66, -34.93) * mm});
            skPoint(sketch, "E16.12.16.0", {"position": v(7.92, -37.27) * mm});
            skPoint(sketch, "E16.13.16.0", {"position": v(7.4, -34.78) * mm});
            skArc(sketch, "E16.14.16.0", {"start": v(11.22, -34.54) * mm, "mid": v(11.26, -33.96) * mm, "end": v(11.7, -33.58) * mm});
            skArc(sketch, "E16.18.16.0", {"start": v(11.76, -36.39) * mm, "mid": v(11.61, -37.54) * mm, "end": v(11.32, -38.68) * mm});
            skPoint(sketch, "E16.22.16.0", {"position": v(11.18, -39.07) * mm});
            skArc(sketch, "E16.23.16.0", {"start": v(8, -37.4) * mm, "mid": v(8.72, -38.32) * mm, "end": v(9.53, -39.15) * mm});
            skPoint(sketch, "E16.24.16.0", {"position": v(11.77, -36.24) * mm});
            skPoint(sketch, "E16.27.16.0", {"position": v(9.85, -39.43) * mm});
            skPoint(sketch, "E16.28.16.0", {"position": v(11.03, -33.8) * mm});
            skLineSegment(sketch, "E16.29.16.0", {"start": v(7.9, -37.13) * mm, "end": v(7.55, -35.52) * mm});
            skArc(sketch, "E16.32.16.0", {"start": v(9.53, -39.15) * mm, "mid": v(9.87, -39.33) * mm, "end": v(10.24, -39.32) * mm});
            skArc(sketch, "E16.36.16.0", {"start": v(10.8, -39.18) * mm, "mid": v(11.12, -39) * mm, "end": v(11.32, -38.68) * mm});
            skLineSegment(sketch, "E16.40.16.0", {"start": v(10.8, -39.18) * mm, "end": v(10.52, -39.25) * mm});
            skLineSegment(sketch, "E16.43.16.0", {"start": v(10.24, -39.32) * mm, "end": v(10.52, -39.25) * mm});
            skArc(sketch, "E16.46.16.0", {"start": v(11.76, -36.39) * mm, "mid": v(11.76, -36.24) * mm, "end": v(11.73, -36.1) * mm});
            skArc(sketch, "E16.50.16.0", {"start": v(7.9, -37.13) * mm, "mid": v(7.94, -37.27) * mm, "end": v(8, -37.4) * mm});
            skArc(sketch, "E16.1.17.0", {"start": v(13.78, -32.78) * mm, "mid": v(16.16, -31.67) * mm, "end": v(18.46, -30.4) * mm});
            skLineSegment(sketch, "E16.5.17.0", {"start": v(18.98, -32.87) * mm, "end": v(18.16, -31.45) * mm});
            skArc(sketch, "E16.8.17.0", {"start": v(14.77, -33.17) * mm, "mid": v(14.35, -32.78) * mm, "end": v(13.78, -32.78) * mm});
            skPoint(sketch, "E16.12.17.0", {"position": v(15.5, -34.8) * mm});
            skPoint(sketch, "E16.13.17.0", {"position": v(14.46, -32.49) * mm});
            skArc(sketch, "E16.14.17.0", {"start": v(18.16, -31.45) * mm, "mid": v(18.08, -30.88) * mm, "end": v(18.42, -30.42) * mm});
            skArc(sketch, "E16.18.17.0", {"start": v(19.07, -33.14) * mm, "mid": v(19.16, -34.3) * mm, "end": v(19.11, -35.48) * mm});
            skPoint(sketch, "E16.22.17.0", {"position": v(19.06, -35.9) * mm});
            skArc(sketch, "E16.23.17.0", {"start": v(15.6, -34.91) * mm, "mid": v(16.5, -35.67) * mm, "end": v(17.47, -36.32) * mm});
            skPoint(sketch, "E16.24.17.0", {"position": v(19.05, -33) * mm});
            skPoint(sketch, "E16.27.17.0", {"position": v(17.83, -36.52) * mm});
            skPoint(sketch, "E16.28.17.0", {"position": v(17.82, -30.77) * mm});
            skLineSegment(sketch, "E16.29.17.0", {"start": v(15.44, -34.67) * mm, "end": v(14.77, -33.17) * mm});
            skArc(sketch, "E16.32.17.0", {"start": v(17.47, -36.32) * mm, "mid": v(17.83, -36.42) * mm, "end": v(18.2, -36.34) * mm});
            skArc(sketch, "E16.36.17.0", {"start": v(18.7, -36.08) * mm, "mid": v(18.98, -35.83) * mm, "end": v(19.11, -35.48) * mm});
            skLineSegment(sketch, "E16.40.17.0", {"start": v(18.7, -36.08) * mm, "end": v(18.45, -36.2) * mm});
            skLineSegment(sketch, "E16.43.17.0", {"start": v(18.2, -36.34) * mm, "end": v(18.45, -36.2) * mm});
            skArc(sketch, "E16.46.17.0", {"start": v(19.07, -33.14) * mm, "mid": v(19.04, -33) * mm, "end": v(18.98, -32.87) * mm});
            skArc(sketch, "E16.50.17.0", {"start": v(15.44, -34.67) * mm, "mid": v(15.5, -34.8) * mm, "end": v(15.6, -34.91) * mm});
            skArc(sketch, "E16.1.18.0", {"start": v(20.3, -29.2) * mm, "mid": v(22.4, -27.62) * mm, "end": v(24.37, -25.9) * mm});
            skLineSegment(sketch, "E16.5.18.0", {"start": v(25.4, -28.2) * mm, "end": v(24.3, -26.99) * mm});
            skArc(sketch, "E16.8.18.0", {"start": v(21.34, -29.38) * mm, "mid": v(20.86, -29.08) * mm, "end": v(20.3, -29.2) * mm});
            skPoint(sketch, "E16.12.18.0", {"position": v(22.4, -30.82) * mm});
            skPoint(sketch, "E16.13.18.0", {"position": v(20.9, -28.77) * mm});
            skArc(sketch, "E16.14.18.0", {"start": v(24.3, -26.99) * mm, "mid": v(24.1, -26.44) * mm, "end": v(24.34, -25.92) * mm});
            skArc(sketch, "E16.18.18.0", {"start": v(25.55, -28.45) * mm, "mid": v(25.88, -29.57) * mm, "end": v(26.07, -30.73) * mm});
            skPoint(sketch, "E16.22.18.0", {"position": v(26.1, -31.15) * mm});
            skArc(sketch, "E16.23.18.0", {"start": v(22.52, -30.9) * mm, "mid": v(23.55, -31.46) * mm, "end": v(24.63, -31.9) * mm});
            skPoint(sketch, "E16.24.18.0", {"position": v(25.5, -28.31) * mm});
            skPoint(sketch, "E16.27.18.0", {"position": v(25.04, -32.01) * mm});
            skPoint(sketch, "E16.28.18.0", {"position": v(23.83, -26.4) * mm});
            skLineSegment(sketch, "E16.29.18.0", {"start": v(22.3, -30.7) * mm, "end": v(21.34, -29.38) * mm});
            skArc(sketch, "E16.32.18.0", {"start": v(24.63, -31.9) * mm, "mid": v(25, -31.92) * mm, "end": v(25.35, -31.76) * mm});
            skArc(sketch, "E16.36.18.0", {"start": v(25.8, -31.4) * mm, "mid": v(26.02, -31.1) * mm, "end": v(26.07, -30.73) * mm});
            skLineSegment(sketch, "E16.40.18.0", {"start": v(25.8, -31.4) * mm, "end": v(25.57, -31.58) * mm});
            skLineSegment(sketch, "E16.43.18.0", {"start": v(25.35, -31.76) * mm, "end": v(25.57, -31.58) * mm});
            skArc(sketch, "E16.46.18.0", {"start": v(25.55, -28.45) * mm, "mid": v(25.48, -28.32) * mm, "end": v(25.4, -28.2) * mm});
            skArc(sketch, "E16.50.18.0", {"start": v(22.3, -30.7) * mm, "mid": v(22.4, -30.82) * mm, "end": v(22.52, -30.9) * mm});
            skArc(sketch, "E16.1.19.0", {"start": v(25.92, -24.34) * mm, "mid": v(27.65, -22.36) * mm, "end": v(29.22, -20.26) * mm});
            skLineSegment(sketch, "E16.5.19.0", {"start": v(30.7, -22.3) * mm, "end": v(29.38, -21.34) * mm});
            skArc(sketch, "E16.8.19.0", {"start": v(26.99, -24.3) * mm, "mid": v(26.44, -24.1) * mm, "end": v(25.92, -24.34) * mm});
            skPoint(sketch, "E16.12.19.0", {"position": v(28.31, -25.5) * mm});
            skPoint(sketch, "E16.13.19.0", {"position": v(26.43, -23.8) * mm});
            skArc(sketch, "E16.14.19.0", {"start": v(29.38, -21.34) * mm, "mid": v(29.08, -20.86) * mm, "end": v(29.2, -20.3) * mm});
            skArc(sketch, "E16.18.19.0", {"start": v(30.9, -22.52) * mm, "mid": v(31.46, -23.55) * mm, "end": v(31.9, -24.63) * mm});
            skPoint(sketch, "E16.22.19.0", {"position": v(32.01, -25.04) * mm});
            skArc(sketch, "E16.23.19.0", {"start": v(28.45, -25.55) * mm, "mid": v(29.57, -25.88) * mm, "end": v(30.73, -26.07) * mm});
            skPoint(sketch, "E16.24.19.0", {"position": v(30.82, -22.4) * mm});
            skPoint(sketch, "E16.27.19.0", {"position": v(31.15, -26.1) * mm});
            skPoint(sketch, "E16.28.19.0", {"position": v(28.8, -20.87) * mm});
            skLineSegment(sketch, "E16.29.19.0", {"start": v(28.2, -25.4) * mm, "end": v(26.99, -24.3) * mm});
            skArc(sketch, "E16.32.19.0", {"start": v(30.73, -26.07) * mm, "mid": v(31.1, -26.02) * mm, "end": v(31.4, -25.8) * mm});
            skArc(sketch, "E16.36.19.0", {"start": v(31.76, -25.35) * mm, "mid": v(31.92, -25) * mm, "end": v(31.9, -24.63) * mm});
            skLineSegment(sketch, "E16.40.19.0", {"start": v(31.76, -25.35) * mm, "end": v(31.58, -25.57) * mm});
            skLineSegment(sketch, "E16.43.19.0", {"start": v(31.4, -25.8) * mm, "end": v(31.58, -25.57) * mm});
            skArc(sketch, "E16.46.19.0", {"start": v(30.9, -22.52) * mm, "mid": v(30.82, -22.4) * mm, "end": v(30.7, -22.3) * mm});
            skArc(sketch, "E16.50.19.0", {"start": v(28.2, -25.4) * mm, "mid": v(28.32, -25.48) * mm, "end": v(28.45, -25.55) * mm});
            skArc(sketch, "E16.1.20.0", {"start": v(30.42, -18.42) * mm, "mid": v(31.7, -16.13) * mm, "end": v(32.8, -13.74) * mm});
            skLineSegment(sketch, "E16.5.20.0", {"start": v(34.67, -15.44) * mm, "end": v(33.17, -14.77) * mm});
            skArc(sketch, "E16.8.20.0", {"start": v(31.45, -18.16) * mm, "mid": v(30.88, -18.08) * mm, "end": v(30.42, -18.42) * mm});
            skPoint(sketch, "E16.12.20.0", {"position": v(33, -19.05) * mm});
            skPoint(sketch, "E16.13.20.0", {"position": v(30.8, -17.78) * mm});
            skArc(sketch, "E16.14.20.0", {"start": v(33.17, -14.77) * mm, "mid": v(32.78, -14.35) * mm, "end": v(32.78, -13.78) * mm});
            skArc(sketch, "E16.18.20.0", {"start": v(34.91, -15.6) * mm, "mid": v(35.67, -16.5) * mm, "end": v(36.32, -17.47) * mm});
            skPoint(sketch, "E16.22.20.0", {"position": v(36.52, -17.83) * mm});
            skArc(sketch, "E16.23.20.0", {"start": v(33.14, -19.07) * mm, "mid": v(34.3, -19.16) * mm, "end": v(35.48, -19.11) * mm});
            skPoint(sketch, "E16.24.20.0", {"position": v(34.8, -15.5) * mm});
            skPoint(sketch, "E16.27.20.0", {"position": v(35.9, -19.06) * mm});
            skPoint(sketch, "E16.28.20.0", {"position": v(32.5, -14.42) * mm});
            skLineSegment(sketch, "E16.29.20.0", {"start": v(32.87, -18.98) * mm, "end": v(31.45, -18.16) * mm});
            skArc(sketch, "E16.32.20.0", {"start": v(35.48, -19.11) * mm, "mid": v(35.83, -18.98) * mm, "end": v(36.08, -18.7) * mm});
            skArc(sketch, "E16.36.20.0", {"start": v(36.34, -18.2) * mm, "mid": v(36.42, -17.83) * mm, "end": v(36.32, -17.47) * mm});
            skLineSegment(sketch, "E16.40.20.0", {"start": v(36.34, -18.2) * mm, "end": v(36.2, -18.45) * mm});
            skLineSegment(sketch, "E16.43.20.0", {"start": v(36.08, -18.7) * mm, "end": v(36.2, -18.45) * mm});
            skArc(sketch, "E16.46.20.0", {"start": v(34.91, -15.6) * mm, "mid": v(34.8, -15.5) * mm, "end": v(34.67, -15.44) * mm});
            skArc(sketch, "E16.50.20.0", {"start": v(32.87, -18.98) * mm, "mid": v(33, -19.04) * mm, "end": v(33.14, -19.07) * mm});
            skArc(sketch, "E16.1.21.0", {"start": v(33.58, -11.7) * mm, "mid": v(34.35, -9.18) * mm, "end": v(34.94, -6.62) * mm});
            skLineSegment(sketch, "E16.5.21.0", {"start": v(37.13, -7.9) * mm, "end": v(35.52, -7.55) * mm});
            skArc(sketch, "E16.8.21.0", {"start": v(34.54, -11.22) * mm, "mid": v(33.96, -11.26) * mm, "end": v(33.58, -11.7) * mm});
            skPoint(sketch, "E16.12.21.0", {"position": v(36.24, -11.77) * mm});
            skPoint(sketch, "E16.13.21.0", {"position": v(33.82, -10.99) * mm});
            skArc(sketch, "E16.14.21.0", {"start": v(35.52, -7.55) * mm, "mid": v(35.04, -7.23) * mm, "end": v(34.93, -6.66) * mm});
            skArc(sketch, "E16.18.21.0", {"start": v(37.4, -8) * mm, "mid": v(38.32, -8.72) * mm, "end": v(39.15, -9.53) * mm});
            skPoint(sketch, "E16.22.21.0", {"position": v(39.43, -9.85) * mm});
            skArc(sketch, "E16.23.21.0", {"start": v(36.39, -11.76) * mm, "mid": v(37.54, -11.61) * mm, "end": v(38.68, -11.32) * mm});
            skPoint(sketch, "E16.24.21.0", {"position": v(37.27, -7.92) * mm});
            skPoint(sketch, "E16.27.21.0", {"position": v(39.07, -11.18) * mm});
            skPoint(sketch, "E16.28.21.0", {"position": v(34.8, -7.35) * mm});
            skLineSegment(sketch, "E16.29.21.0", {"start": v(36.1, -11.73) * mm, "end": v(34.54, -11.22) * mm});
            skArc(sketch, "E16.32.21.0", {"start": v(38.68, -11.32) * mm, "mid": v(39, -11.12) * mm, "end": v(39.18, -10.8) * mm});
            skArc(sketch, "E16.36.21.0", {"start": v(39.32, -10.24) * mm, "mid": v(39.33, -9.87) * mm, "end": v(39.15, -9.53) * mm});
            skLineSegment(sketch, "E16.40.21.0", {"start": v(39.32, -10.24) * mm, "end": v(39.25, -10.52) * mm});
            skLineSegment(sketch, "E16.43.21.0", {"start": v(39.18, -10.8) * mm, "end": v(39.25, -10.52) * mm});
            skArc(sketch, "E16.46.21.0", {"start": v(37.4, -8) * mm, "mid": v(37.27, -7.94) * mm, "end": v(37.13, -7.9) * mm});
            skArc(sketch, "E16.50.21.0", {"start": v(36.1, -11.73) * mm, "mid": v(36.24, -11.76) * mm, "end": v(36.39, -11.76) * mm});
            skArc(sketch, "E16.1.22.0", {"start": v(35.28, -4.46) * mm, "mid": v(35.51, -1.84) * mm, "end": v(35.55, 0.79) * mm});
            skLineSegment(sketch, "E16.5.22.0", {"start": v(37.96, 0) * mm, "end": v(36.31, 0) * mm});
            skArc(sketch, "E16.8.22.0", {"start": v(36.12, -3.8) * mm, "mid": v(35.56, -3.96) * mm, "end": v(35.28, -4.46) * mm});
            skPoint(sketch, "E16.12.22.0", {"position": v(37.9, -3.98) * mm});
            skPoint(sketch, "E16.13.22.0", {"position": v(35.37, -3.72) * mm});
            skArc(sketch, "E16.14.22.0", {"start": v(36.31, 0) * mm, "mid": v(35.78, 0.22) * mm, "end": v(35.55, 0.75) * mm});
            skArc(sketch, "E16.18.22.0", {"start": v(38.24, -0.06) * mm, "mid": v(39.3, -0.56) * mm, "end": v(40.28, -1.18) * mm});
            skPoint(sketch, "E16.22.22.0", {"position": v(40.61, -1.44) * mm});
            skArc(sketch, "E16.23.22.0", {"start": v(38.04, -3.94) * mm, "mid": v(39.14, -3.55) * mm, "end": v(40.18, -3.03) * mm});
            skPoint(sketch, "E16.24.22.0", {"position": v(38.1, 0) * mm});
            skPoint(sketch, "E16.27.22.0", {"position": v(40.54, -2.81) * mm});
            skPoint(sketch, "E16.28.22.0", {"position": v(35.56, 0.04) * mm});
            skLineSegment(sketch, "E16.29.22.0", {"start": v(37.75, -3.97) * mm, "end": v(36.12, -3.8) * mm});
            skArc(sketch, "E16.32.22.0", {"start": v(40.18, -3.03) * mm, "mid": v(40.45, -2.77) * mm, "end": v(40.56, -2.41) * mm});
            skArc(sketch, "E16.36.22.0", {"start": v(40.6, -1.84) * mm, "mid": v(40.52, -1.47) * mm, "end": v(40.28, -1.18) * mm});
            skLineSegment(sketch, "E16.40.22.0", {"start": v(40.6, -1.84) * mm, "end": v(40.58, -2.13) * mm});
            skLineSegment(sketch, "E16.43.22.0", {"start": v(40.56, -2.41) * mm, "end": v(40.58, -2.13) * mm});
            skArc(sketch, "E16.46.22.0", {"start": v(38.24, -0.06) * mm, "mid": v(38.1, -0.01) * mm, "end": v(37.96, 0) * mm});
            skArc(sketch, "E16.50.22.0", {"start": v(37.75, -3.97) * mm, "mid": v(37.9, -3.97) * mm, "end": v(38.04, -3.94) * mm});
            skArc(sketch, "E16.1.23.0", {"start": v(35.44, 2.97) * mm, "mid": v(35.12, 5.58) * mm, "end": v(34.61, 8.16) * mm});
            skLineSegment(sketch, "E16.5.23.0", {"start": v(37.13, 7.9) * mm, "end": v(35.52, 7.55) * mm});
            skArc(sketch, "E16.8.23.0", {"start": v(36.12, 3.8) * mm, "mid": v(35.6, 3.52) * mm, "end": v(35.44, 2.97) * mm});
            skPoint(sketch, "E16.12.23.0", {"position": v(37.9, 3.98) * mm});
            skPoint(sketch, "E16.13.23.0", {"position": v(35.37, 3.72) * mm});
            skArc(sketch, "E16.14.23.0", {"start": v(35.52, 7.55) * mm, "mid": v(34.95, 7.65) * mm, "end": v(34.62, 8.12) * mm});
            skArc(sketch, "E16.18.23.0", {"start": v(37.42, 7.9) * mm, "mid": v(38.55, 7.62) * mm, "end": v(39.65, 7.22) * mm});
            skPoint(sketch, "E16.22.23.0", {"position": v(40.03, 7.04) * mm});
            skArc(sketch, "E16.23.23.0", {"start": v(38.02, 4.05) * mm, "mid": v(39.02, 4.66) * mm, "end": v(39.94, 5.39) * mm});
            skPoint(sketch, "E16.24.23.0", {"position": v(37.27, 7.92) * mm});
            skPoint(sketch, "E16.27.23.0", {"position": v(40.24, 5.68) * mm});
            skPoint(sketch, "E16.28.23.0", {"position": v(34.77, 7.43) * mm});
            skLineSegment(sketch, "E16.29.23.0", {"start": v(37.75, 3.97) * mm, "end": v(36.12, 3.8) * mm});
            skArc(sketch, "E16.32.23.0", {"start": v(39.94, 5.39) * mm, "mid": v(40.14, 5.7) * mm, "end": v(40.18, 6.07) * mm});
            skArc(sketch, "E16.36.23.0", {"start": v(40.09, 6.64) * mm, "mid": v(39.94, 6.98) * mm, "end": v(39.65, 7.22) * mm});
            skLineSegment(sketch, "E16.40.23.0", {"start": v(40.09, 6.64) * mm, "end": v(40.13, 6.36) * mm});
            skLineSegment(sketch, "E16.43.23.0", {"start": v(40.18, 6.07) * mm, "end": v(40.13, 6.36) * mm});
            skArc(sketch, "E16.46.23.0", {"start": v(37.42, 7.9) * mm, "mid": v(37.27, 7.9) * mm, "end": v(37.13, 7.9) * mm});
            skArc(sketch, "E16.50.23.0", {"start": v(37.75, 3.97) * mm, "mid": v(37.9, 4) * mm, "end": v(38.02, 4.05) * mm});
            skArc(sketch, "E16.1.24.0", {"start": v(34.04, 10.28) * mm, "mid": v(33.2, 12.76) * mm, "end": v(32.16, 15.18) * mm});
            skLineSegment(sketch, "E16.5.24.0", {"start": v(34.67, 15.44) * mm, "end": v(33.17, 14.77) * mm});
            skArc(sketch, "E16.8.24.0", {"start": v(34.54, 11.22) * mm, "mid": v(34.1, 10.85) * mm, "end": v(34.04, 10.28) * mm});
            skPoint(sketch, "E16.12.24.0", {"position": v(36.24, 11.77) * mm});
            skPoint(sketch, "E16.13.24.0", {"position": v(33.82, 10.99) * mm});
            skArc(sketch, "E16.14.24.0", {"start": v(33.17, 14.77) * mm, "mid": v(32.6, 14.75) * mm, "end": v(32.18, 15.14) * mm});
            skArc(sketch, "E16.18.24.0", {"start": v(34.96, 15.5) * mm, "mid": v(36.12, 15.47) * mm, "end": v(37.28, 15.3) * mm});
            skPoint(sketch, "E16.22.24.0", {"position": v(37.69, 15.2) * mm});
            skArc(sketch, "E16.23.24.0", {"start": v(36.35, 11.87) * mm, "mid": v(37.2, 12.67) * mm, "end": v(37.94, 13.57) * mm});
            skPoint(sketch, "E16.24.24.0", {"position": v(34.8, 15.5) * mm});
            skPoint(sketch, "E16.27.24.0", {"position": v(38.18, 13.92) * mm});
            skPoint(sketch, "E16.28.24.0", {"position": v(32.47, 14.5) * mm});
            skLineSegment(sketch, "E16.29.24.0", {"start": v(36.1, 11.73) * mm, "end": v(34.54, 11.22) * mm});
            skArc(sketch, "E16.32.24.0", {"start": v(37.94, 13.57) * mm, "mid": v(38.08, 13.92) * mm, "end": v(38.04, 14.3) * mm});
            skArc(sketch, "E16.36.24.0", {"start": v(37.83, 14.83) * mm, "mid": v(37.62, 15.14) * mm, "end": v(37.28, 15.3) * mm});
            skLineSegment(sketch, "E16.40.24.0", {"start": v(37.83, 14.83) * mm, "end": v(37.94, 14.56) * mm});
            skLineSegment(sketch, "E16.43.24.0", {"start": v(38.04, 14.3) * mm, "end": v(37.94, 14.56) * mm});
            skArc(sketch, "E16.46.24.0", {"start": v(34.96, 15.5) * mm, "mid": v(34.81, 15.48) * mm, "end": v(34.67, 15.44) * mm});
            skArc(sketch, "E16.50.24.0", {"start": v(36.1, 11.73) * mm, "mid": v(36.23, 11.79) * mm, "end": v(36.35, 11.87) * mm});
            skArc(sketch, "E16.1.25.0", {"start": v(31.16, 17.13) * mm, "mid": v(29.81, 19.38) * mm, "end": v(28.3, 21.53) * mm});
            skLineSegment(sketch, "E16.5.25.0", {"start": v(30.7, 22.3) * mm, "end": v(29.38, 21.34) * mm});
            skArc(sketch, "E16.8.25.0", {"start": v(31.45, 18.16) * mm, "mid": v(31.1, 17.7) * mm, "end": v(31.16, 17.13) * mm});
            skPoint(sketch, "E16.12.25.0", {"position": v(33, 19.05) * mm});
            skPoint(sketch, "E16.13.25.0", {"position": v(30.8, 17.78) * mm});
            skArc(sketch, "E16.14.25.0", {"start": v(29.38, 21.34) * mm, "mid": v(28.82, 21.2) * mm, "end": v(28.32, 21.5) * mm});
            skArc(sketch, "E16.18.25.0", {"start": v(30.97, 22.43) * mm, "mid": v(32.12, 22.65) * mm, "end": v(33.28, 22.72) * mm});
            skPoint(sketch, "E16.22.25.0", {"position": v(33.7, 22.7) * mm});
            skArc(sketch, "E16.23.25.0", {"start": v(33.09, 19.17) * mm, "mid": v(33.75, 20.13) * mm, "end": v(34.3, 21.17) * mm});
            skPoint(sketch, "E16.24.25.0", {"position": v(30.82, 22.4) * mm});
            skPoint(sketch, "E16.27.25.0", {"position": v(34.45, 21.55) * mm});
            skPoint(sketch, "E16.28.25.0", {"position": v(28.74, 20.94) * mm});
            skLineSegment(sketch, "E16.29.25.0", {"start": v(32.87, 18.98) * mm, "end": v(31.45, 18.16) * mm});
            skArc(sketch, "E16.32.25.0", {"start": v(34.3, 21.17) * mm, "mid": v(34.35, 21.54) * mm, "end": v(34.23, 21.9) * mm});
            skArc(sketch, "E16.36.25.0", {"start": v(33.92, 22.37) * mm, "mid": v(33.65, 22.63) * mm, "end": v(33.28, 22.72) * mm});
            skLineSegment(sketch, "E16.40.25.0", {"start": v(33.92, 22.37) * mm, "end": v(34.08, 22.13) * mm});
            skLineSegment(sketch, "E16.43.25.0", {"start": v(34.23, 21.9) * mm, "end": v(34.08, 22.13) * mm});
            skArc(sketch, "E16.46.25.0", {"start": v(30.97, 22.43) * mm, "mid": v(30.83, 22.38) * mm, "end": v(30.7, 22.3) * mm});
            skArc(sketch, "E16.50.25.0", {"start": v(32.87, 18.98) * mm, "mid": v(32.99, 19.06) * mm, "end": v(33.09, 19.17) * mm});
            skArc(sketch, "E16.1.26.0", {"start": v(26.92, 23.23) * mm, "mid": v(25.13, 25.16) * mm, "end": v(23.2, 26.95) * mm});
            skLineSegment(sketch, "E16.5.26.0", {"start": v(25.4, 28.2) * mm, "end": v(24.3, 26.99) * mm});
            skArc(sketch, "E16.8.26.0", {"start": v(26.99, 24.3) * mm, "mid": v(26.74, 23.78) * mm, "end": v(26.92, 23.23) * mm});
            skPoint(sketch, "E16.12.26.0", {"position": v(28.31, 25.5) * mm});
            skPoint(sketch, "E16.13.26.0", {"position": v(26.43, 23.8) * mm});
            skArc(sketch, "E16.14.26.0", {"start": v(24.3, 26.99) * mm, "mid": v(23.78, 26.74) * mm, "end": v(23.23, 26.92) * mm});
            skArc(sketch, "E16.18.26.0", {"start": v(25.63, 28.38) * mm, "mid": v(26.7, 28.83) * mm, "end": v(27.83, 29.14) * mm});
            skPoint(sketch, "E16.22.26.0", {"position": v(28.25, 29.22) * mm});
            skArc(sketch, "E16.23.26.0", {"start": v(28.38, 25.63) * mm, "mid": v(28.83, 26.7) * mm, "end": v(29.14, 27.83) * mm});
            skPoint(sketch, "E16.24.26.0", {"position": v(25.5, 28.31) * mm});
            skPoint(sketch, "E16.27.26.0", {"position": v(29.22, 28.25) * mm});
            skPoint(sketch, "E16.28.26.0", {"position": v(23.76, 26.45) * mm});
            skLineSegment(sketch, "E16.29.26.0", {"start": v(28.2, 25.4) * mm, "end": v(26.99, 24.3) * mm});
            skArc(sketch, "E16.32.26.0", {"start": v(29.14, 27.83) * mm, "mid": v(29.13, 28.2) * mm, "end": v(28.93, 28.53) * mm});
            skArc(sketch, "E16.36.26.0", {"start": v(28.53, 28.93) * mm, "mid": v(28.2, 29.13) * mm, "end": v(27.83, 29.14) * mm});
            skLineSegment(sketch, "E16.40.26.0", {"start": v(28.53, 28.93) * mm, "end": v(28.73, 28.73) * mm});
            skLineSegment(sketch, "E16.43.26.0", {"start": v(28.93, 28.53) * mm, "end": v(28.73, 28.73) * mm});
            skArc(sketch, "E16.46.26.0", {"start": v(25.63, 28.38) * mm, "mid": v(25.5, 28.3) * mm, "end": v(25.4, 28.2) * mm});
            skArc(sketch, "E16.50.26.0", {"start": v(28.2, 25.4) * mm, "mid": v(28.3, 25.5) * mm, "end": v(28.38, 25.63) * mm});
            skArc(sketch, "E16.1.27.0", {"start": v(21.5, 28.32) * mm, "mid": v(19.35, 29.83) * mm, "end": v(17.1, 31.18) * mm});
            skLineSegment(sketch, "E16.5.27.0", {"start": v(18.98, 32.87) * mm, "end": v(18.16, 31.45) * mm});
            skArc(sketch, "E16.8.27.0", {"start": v(21.34, 29.38) * mm, "mid": v(21.2, 28.82) * mm, "end": v(21.5, 28.32) * mm});
            skPoint(sketch, "E16.12.27.0", {"position": v(22.4, 30.82) * mm});
            skPoint(sketch, "E16.13.27.0", {"position": v(20.9, 28.77) * mm});
            skArc(sketch, "E16.14.27.0", {"start": v(18.16, 31.45) * mm, "mid": v(17.7, 31.1) * mm, "end": v(17.13, 31.16) * mm});
            skArc(sketch, "E16.18.27.0", {"start": v(19.17, 33.09) * mm, "mid": v(20.13, 33.75) * mm, "end": v(21.17, 34.3) * mm});
            skPoint(sketch, "E16.22.27.0", {"position": v(21.55, 34.45) * mm});
            skArc(sketch, "E16.23.27.0", {"start": v(22.43, 30.97) * mm, "mid": v(22.65, 32.12) * mm, "end": v(22.72, 33.28) * mm});
            skPoint(sketch, "E16.24.27.0", {"position": v(19.05, 33) * mm});
            skPoint(sketch, "E16.27.27.0", {"position": v(22.7, 33.7) * mm});
            skPoint(sketch, "E16.28.27.0", {"position": v(17.74, 30.82) * mm});
            skLineSegment(sketch, "E16.29.27.0", {"start": v(22.3, 30.7) * mm, "end": v(21.34, 29.38) * mm});
            skArc(sketch, "E16.32.27.0", {"start": v(22.72, 33.28) * mm, "mid": v(22.63, 33.65) * mm, "end": v(22.37, 33.92) * mm});
            skArc(sketch, "E16.36.27.0", {"start": v(21.9, 34.23) * mm, "mid": v(21.54, 34.35) * mm, "end": v(21.17, 34.3) * mm});
            skLineSegment(sketch, "E16.40.27.0", {"start": v(21.9, 34.23) * mm, "end": v(22.13, 34.08) * mm});
            skLineSegment(sketch, "E16.43.27.0", {"start": v(22.37, 33.92) * mm, "end": v(22.13, 34.08) * mm});
            skArc(sketch, "E16.46.27.0", {"start": v(19.17, 33.09) * mm, "mid": v(19.06, 32.99) * mm, "end": v(18.98, 32.87) * mm});
            skArc(sketch, "E16.50.27.0", {"start": v(22.3, 30.7) * mm, "mid": v(22.38, 30.83) * mm, "end": v(22.43, 30.97) * mm});
            skArc(sketch, "E16.1.28.0", {"start": v(15.14, 32.18) * mm, "mid": v(12.72, 33.2) * mm, "end": v(10.24, 34.05) * mm});
            skLineSegment(sketch, "E16.5.28.0", {"start": v(11.73, 36.1) * mm, "end": v(11.22, 34.54) * mm});
            skArc(sketch, "E16.8.28.0", {"start": v(14.77, 33.17) * mm, "mid": v(14.75, 32.6) * mm, "end": v(15.14, 32.18) * mm});
            skPoint(sketch, "E16.12.28.0", {"position": v(15.5, 34.8) * mm});
            skPoint(sketch, "E16.13.28.0", {"position": v(14.46, 32.49) * mm});
            skArc(sketch, "E16.14.28.0", {"start": v(11.22, 34.54) * mm, "mid": v(10.85, 34.1) * mm, "end": v(10.28, 34.04) * mm});
            skArc(sketch, "E16.18.28.0", {"start": v(11.87, 36.35) * mm, "mid": v(12.67, 37.2) * mm, "end": v(13.57, 37.94) * mm});
            skPoint(sketch, "E16.22.28.0", {"position": v(13.92, 38.18) * mm});
            skArc(sketch, "E16.23.28.0", {"start": v(15.5, 34.96) * mm, "mid": v(15.47, 36.12) * mm, "end": v(15.3, 37.28) * mm});
            skPoint(sketch, "E16.24.28.0", {"position": v(11.77, 36.24) * mm});
            skPoint(sketch, "E16.27.28.0", {"position": v(15.2, 37.69) * mm});
            skPoint(sketch, "E16.28.28.0", {"position": v(10.95, 33.83) * mm});
            skLineSegment(sketch, "E16.29.28.0", {"start": v(15.44, 34.67) * mm, "end": v(14.77, 33.17) * mm});
            skArc(sketch, "E16.32.28.0", {"start": v(15.3, 37.28) * mm, "mid": v(15.14, 37.62) * mm, "end": v(14.83, 37.83) * mm});
            skArc(sketch, "E16.36.28.0", {"start": v(14.3, 38.04) * mm, "mid": v(13.92, 38.08) * mm, "end": v(13.57, 37.94) * mm});
            skLineSegment(sketch, "E16.40.28.0", {"start": v(14.3, 38.04) * mm, "end": v(14.56, 37.94) * mm});
            skLineSegment(sketch, "E16.43.28.0", {"start": v(14.83, 37.83) * mm, "end": v(14.56, 37.94) * mm});
            skArc(sketch, "E16.46.28.0", {"start": v(11.87, 36.35) * mm, "mid": v(11.79, 36.23) * mm, "end": v(11.73, 36.1) * mm});
            skArc(sketch, "E16.50.28.0", {"start": v(15.44, 34.67) * mm, "mid": v(15.48, 34.81) * mm, "end": v(15.5, 34.96) * mm});
            skArc(sketch, "E16.1.29.0", {"start": v(8.12, 34.62) * mm, "mid": v(5.54, 35.13) * mm, "end": v(2.93, 35.44) * mm});
            skLineSegment(sketch, "E16.5.29.0", {"start": v(3.97, 37.75) * mm, "end": v(3.8, 36.12) * mm});
            skArc(sketch, "E16.8.29.0", {"start": v(7.55, 35.52) * mm, "mid": v(7.65, 34.95) * mm, "end": v(8.12, 34.62) * mm});
            skPoint(sketch, "E16.12.29.0", {"position": v(7.92, 37.27) * mm});
            skPoint(sketch, "E16.13.29.0", {"position": v(7.4, 34.78) * mm});
            skArc(sketch, "E16.14.29.0", {"start": v(3.8, 36.12) * mm, "mid": v(3.52, 35.6) * mm, "end": v(2.97, 35.44) * mm});
            skArc(sketch, "E16.18.29.0", {"start": v(4.05, 38.02) * mm, "mid": v(4.66, 39.02) * mm, "end": v(5.39, 39.94) * mm});
            skPoint(sketch, "E16.22.29.0", {"position": v(5.68, 40.24) * mm});
            skArc(sketch, "E16.23.29.0", {"start": v(7.9, 37.42) * mm, "mid": v(7.62, 38.55) * mm, "end": v(7.22, 39.65) * mm});
            skPoint(sketch, "E16.24.29.0", {"position": v(3.98, 37.9) * mm});
            skPoint(sketch, "E16.27.29.0", {"position": v(7.04, 40.03) * mm});
            skPoint(sketch, "E16.28.29.0", {"position": v(3.67, 35.37) * mm});
            skLineSegment(sketch, "E16.29.29.0", {"start": v(7.9, 37.13) * mm, "end": v(7.55, 35.52) * mm});
            skArc(sketch, "E16.32.29.0", {"start": v(7.22, 39.65) * mm, "mid": v(6.98, 39.94) * mm, "end": v(6.64, 40.09) * mm});
            skArc(sketch, "E16.36.29.0", {"start": v(6.07, 40.18) * mm, "mid": v(5.7, 40.14) * mm, "end": v(5.39, 39.94) * mm});
            skLineSegment(sketch, "E16.40.29.0", {"start": v(6.07, 40.18) * mm, "end": v(6.36, 40.13) * mm});
            skLineSegment(sketch, "E16.43.29.0", {"start": v(6.64, 40.09) * mm, "end": v(6.36, 40.13) * mm});
            skArc(sketch, "E16.46.29.0", {"start": v(4.05, 38.02) * mm, "mid": v(4, 37.9) * mm, "end": v(3.97, 37.75) * mm});
            skArc(sketch, "E16.50.29.0", {"start": v(7.9, 37.13) * mm, "mid": v(7.9, 37.27) * mm, "end": v(7.9, 37.42) * mm});
            skSolve(sketch);
        }
        {
            var Q0;
            Q0=qSketchRegion(id+"F3",true);
            extrude(context, id + "F4", {"entities" : qUnion([Q0]), "operationType" : NewBodyOperationType.ADD, "oppositeDirection" : true, "depth" : 57.15 * mm});
        }
        {
            var Q0;
            Q0=makeQuery(id+"F4.opExtrude","CAP_FACE",FACE,{"disambiguationData":[OSD([sQuery(id+"F3.wireOp",EDGE,"E1.trimOffspring"),sQuery(id+"F3.wireOp",EDGE,"E2"),sQuery(id+"F3.wireOp",EDGE,"E3"),sQuery(id+"F3.wireOp",EDGE,"E4.MirrorCS"),sQuery(id+"F3.wireOp",EDGE,"E5.MirrorCS"),sQuery(id+"F3.wireOp",EDGE,"E7.filletArc"),sQuery(id+"F3.wireOp",EDGE,"E8"),sQuery(id+"F3.wireOp",EDGE,"E9.MirrorCS"),sQuery(id+"F3.wireOp",EDGE,"E10.MirrorCS"),sQuery(id+"F3.wireOp",EDGE,"E11.filletArc"),sQuery(id+"F3.wireOp",EDGE,"E12.filletArc"),sQuery(id+"F3.wireOp",EDGE,"E13.filletArc"),sQuery(id+"F3.wireOp",EDGE,"E14.filletArc")])],"isStart":false});
            var Q1;
            Q1=makeQuery(id+"F4.opExtrude","CAP_FACE",FACE,{"disambiguationData":[OSD([sQuery(id+"F3.wireOp",EDGE,"E15.1.1"),sQuery(id+"F3.wireOp",EDGE,"E15.1.2"),sQuery(id+"F3.wireOp",EDGE,"E15.1.3"),sQuery(id+"F3.wireOp",EDGE,"E15.1.6"),sQuery(id+"F3.wireOp",EDGE,"E15.1.7"),sQuery(id+"F3.wireOp",EDGE,"E15.1.9"),sQuery(id+"F3.wireOp",EDGE,"E15.1.12"),sQuery(id+"F3.wireOp",EDGE,"E15.1.13"),sQuery(id+"F3.wireOp",EDGE,"E15.1.14"),sQuery(id+"F3.wireOp",EDGE,"E15.1.15"),sQuery(id+"F3.wireOp",EDGE,"E15.1.16"),sQuery(id+"F3.wireOp",EDGE,"E15.1.17"),sQuery(id+"F3.wireOp",EDGE,"E15.1.18")])],"isStart":false});
            var Q2;
            Q2=makeQuery(id+"F4.opExtrude","CAP_FACE",FACE,{"disambiguationData":[OSD([sQuery(id+"F3.wireOp",EDGE,"E16.1.29.0"),sQuery(id+"F3.wireOp",EDGE,"E16.5.29.0"),sQuery(id+"F3.wireOp",EDGE,"E16.8.29.0"),sQuery(id+"F3.wireOp",EDGE,"E16.14.29.0"),sQuery(id+"F3.wireOp",EDGE,"E16.18.29.0"),sQuery(id+"F3.wireOp",EDGE,"E16.23.29.0"),sQuery(id+"F3.wireOp",EDGE,"E16.29.29.0"),sQuery(id+"F3.wireOp",EDGE,"E16.32.29.0"),sQuery(id+"F3.wireOp",EDGE,"E16.36.29.0"),sQuery(id+"F3.wireOp",EDGE,"E16.40.29.0"),sQuery(id+"F3.wireOp",EDGE,"E16.43.29.0"),sQuery(id+"F3.wireOp",EDGE,"E16.46.29.0"),sQuery(id+"F3.wireOp",EDGE,"E16.50.29.0")])],"isStart":false});
            var Q3;
            Q3=makeQuery(id+"F4.opExtrude","CAP_FACE",FACE,{"disambiguationData":[OSD([sQuery(id+"F3.wireOp",EDGE,"E16.1.28.0"),sQuery(id+"F3.wireOp",EDGE,"E16.5.28.0"),sQuery(id+"F3.wireOp",EDGE,"E16.8.28.0"),sQuery(id+"F3.wireOp",EDGE,"E16.14.28.0"),sQuery(id+"F3.wireOp",EDGE,"E16.18.28.0"),sQuery(id+"F3.wireOp",EDGE,"E16.23.28.0"),sQuery(id+"F3.wireOp",EDGE,"E16.29.28.0"),sQuery(id+"F3.wireOp",EDGE,"E16.32.28.0"),sQuery(id+"F3.wireOp",EDGE,"E16.36.28.0"),sQuery(id+"F3.wireOp",EDGE,"E16.40.28.0"),sQuery(id+"F3.wireOp",EDGE,"E16.43.28.0"),sQuery(id+"F3.wireOp",EDGE,"E16.46.28.0"),sQuery(id+"F3.wireOp",EDGE,"E16.50.28.0")])],"isStart":false});
            var Q4;
            Q4=makeQuery(id+"F4.opExtrude","CAP_FACE",FACE,{"disambiguationData":[OSD([sQuery(id+"F3.wireOp",EDGE,"E16.1.27.0"),sQuery(id+"F3.wireOp",EDGE,"E16.5.27.0"),sQuery(id+"F3.wireOp",EDGE,"E16.8.27.0"),sQuery(id+"F3.wireOp",EDGE,"E16.14.27.0"),sQuery(id+"F3.wireOp",EDGE,"E16.18.27.0"),sQuery(id+"F3.wireOp",EDGE,"E16.23.27.0"),sQuery(id+"F3.wireOp",EDGE,"E16.29.27.0"),sQuery(id+"F3.wireOp",EDGE,"E16.32.27.0"),sQuery(id+"F3.wireOp",EDGE,"E16.36.27.0"),sQuery(id+"F3.wireOp",EDGE,"E16.40.27.0"),sQuery(id+"F3.wireOp",EDGE,"E16.43.27.0"),sQuery(id+"F3.wireOp",EDGE,"E16.46.27.0"),sQuery(id+"F3.wireOp",EDGE,"E16.50.27.0")])],"isStart":false});
            var Q5;
            Q5=makeQuery(id+"F4.opExtrude","CAP_FACE",FACE,{"disambiguationData":[OSD([sQuery(id+"F3.wireOp",EDGE,"E16.1.26.0"),sQuery(id+"F3.wireOp",EDGE,"E16.5.26.0"),sQuery(id+"F3.wireOp",EDGE,"E16.8.26.0"),sQuery(id+"F3.wireOp",EDGE,"E16.14.26.0"),sQuery(id+"F3.wireOp",EDGE,"E16.18.26.0"),sQuery(id+"F3.wireOp",EDGE,"E16.23.26.0"),sQuery(id+"F3.wireOp",EDGE,"E16.29.26.0"),sQuery(id+"F3.wireOp",EDGE,"E16.32.26.0"),sQuery(id+"F3.wireOp",EDGE,"E16.36.26.0"),sQuery(id+"F3.wireOp",EDGE,"E16.40.26.0"),sQuery(id+"F3.wireOp",EDGE,"E16.43.26.0"),sQuery(id+"F3.wireOp",EDGE,"E16.46.26.0"),sQuery(id+"F3.wireOp",EDGE,"E16.50.26.0")])],"isStart":false});
            var Q6;
            Q6=makeQuery(id+"F4.opExtrude","CAP_FACE",FACE,{"disambiguationData":[OSD([sQuery(id+"F3.wireOp",EDGE,"E16.1.25.0"),sQuery(id+"F3.wireOp",EDGE,"E16.5.25.0"),sQuery(id+"F3.wireOp",EDGE,"E16.8.25.0"),sQuery(id+"F3.wireOp",EDGE,"E16.14.25.0"),sQuery(id+"F3.wireOp",EDGE,"E16.18.25.0"),sQuery(id+"F3.wireOp",EDGE,"E16.23.25.0"),sQuery(id+"F3.wireOp",EDGE,"E16.29.25.0"),sQuery(id+"F3.wireOp",EDGE,"E16.32.25.0"),sQuery(id+"F3.wireOp",EDGE,"E16.36.25.0"),sQuery(id+"F3.wireOp",EDGE,"E16.40.25.0"),sQuery(id+"F3.wireOp",EDGE,"E16.43.25.0"),sQuery(id+"F3.wireOp",EDGE,"E16.46.25.0"),sQuery(id+"F3.wireOp",EDGE,"E16.50.25.0")])],"isStart":false});
            var Q7;
            Q7=makeQuery(id+"F4.opExtrude","CAP_FACE",FACE,{"disambiguationData":[OSD([sQuery(id+"F3.wireOp",EDGE,"E15.2.1"),sQuery(id+"F3.wireOp",EDGE,"E15.2.2"),sQuery(id+"F3.wireOp",EDGE,"E15.2.3"),sQuery(id+"F3.wireOp",EDGE,"E15.2.6"),sQuery(id+"F3.wireOp",EDGE,"E15.2.7"),sQuery(id+"F3.wireOp",EDGE,"E15.2.9"),sQuery(id+"F3.wireOp",EDGE,"E15.2.12"),sQuery(id+"F3.wireOp",EDGE,"E15.2.13"),sQuery(id+"F3.wireOp",EDGE,"E15.2.14"),sQuery(id+"F3.wireOp",EDGE,"E15.2.15"),sQuery(id+"F3.wireOp",EDGE,"E15.2.16"),sQuery(id+"F3.wireOp",EDGE,"E15.2.17"),sQuery(id+"F3.wireOp",EDGE,"E15.2.18")])],"isStart":false});
            var Q8;
            Q8=makeQuery(id+"F4.opExtrude","CAP_FACE",FACE,{"disambiguationData":[OSD([sQuery(id+"F3.wireOp",EDGE,"E16.1.3.0"),sQuery(id+"F3.wireOp",EDGE,"E16.5.3.0"),sQuery(id+"F3.wireOp",EDGE,"E16.8.3.0"),sQuery(id+"F3.wireOp",EDGE,"E16.14.3.0"),sQuery(id+"F3.wireOp",EDGE,"E16.18.3.0"),sQuery(id+"F3.wireOp",EDGE,"E16.23.3.0"),sQuery(id+"F3.wireOp",EDGE,"E16.29.3.0"),sQuery(id+"F3.wireOp",EDGE,"E16.32.3.0"),sQuery(id+"F3.wireOp",EDGE,"E16.36.3.0"),sQuery(id+"F3.wireOp",EDGE,"E16.40.3.0"),sQuery(id+"F3.wireOp",EDGE,"E16.43.3.0"),sQuery(id+"F3.wireOp",EDGE,"E16.46.3.0"),sQuery(id+"F3.wireOp",EDGE,"E16.50.3.0")])],"isStart":false});
            var Q9;
            Q9=makeQuery(id+"F4.opExtrude","CAP_FACE",FACE,{"disambiguationData":[OSD([sQuery(id+"F3.wireOp",EDGE,"E16.1.4.0"),sQuery(id+"F3.wireOp",EDGE,"E16.5.4.0"),sQuery(id+"F3.wireOp",EDGE,"E16.8.4.0"),sQuery(id+"F3.wireOp",EDGE,"E16.14.4.0"),sQuery(id+"F3.wireOp",EDGE,"E16.18.4.0"),sQuery(id+"F3.wireOp",EDGE,"E16.23.4.0"),sQuery(id+"F3.wireOp",EDGE,"E16.29.4.0"),sQuery(id+"F3.wireOp",EDGE,"E16.32.4.0"),sQuery(id+"F3.wireOp",EDGE,"E16.36.4.0"),sQuery(id+"F3.wireOp",EDGE,"E16.40.4.0"),sQuery(id+"F3.wireOp",EDGE,"E16.43.4.0"),sQuery(id+"F3.wireOp",EDGE,"E16.46.4.0"),sQuery(id+"F3.wireOp",EDGE,"E16.50.4.0")])],"isStart":false});
            var Q10;
            Q10=makeQuery(id+"F4.opExtrude","CAP_FACE",FACE,{"disambiguationData":[OSD([sQuery(id+"F3.wireOp",EDGE,"E16.1.5.0"),sQuery(id+"F3.wireOp",EDGE,"E16.5.5.0"),sQuery(id+"F3.wireOp",EDGE,"E16.8.5.0"),sQuery(id+"F3.wireOp",EDGE,"E16.14.5.0"),sQuery(id+"F3.wireOp",EDGE,"E16.18.5.0"),sQuery(id+"F3.wireOp",EDGE,"E16.23.5.0"),sQuery(id+"F3.wireOp",EDGE,"E16.29.5.0"),sQuery(id+"F3.wireOp",EDGE,"E16.32.5.0"),sQuery(id+"F3.wireOp",EDGE,"E16.36.5.0"),sQuery(id+"F3.wireOp",EDGE,"E16.40.5.0"),sQuery(id+"F3.wireOp",EDGE,"E16.43.5.0"),sQuery(id+"F3.wireOp",EDGE,"E16.46.5.0"),sQuery(id+"F3.wireOp",EDGE,"E16.50.5.0")])],"isStart":false});
            var Q11;
            Q11=makeQuery(id+"F4.opExtrude","CAP_FACE",FACE,{"disambiguationData":[OSD([sQuery(id+"F3.wireOp",EDGE,"E16.1.7.0"),sQuery(id+"F3.wireOp",EDGE,"E16.5.7.0"),sQuery(id+"F3.wireOp",EDGE,"E16.8.7.0"),sQuery(id+"F3.wireOp",EDGE,"E16.14.7.0"),sQuery(id+"F3.wireOp",EDGE,"E16.18.7.0"),sQuery(id+"F3.wireOp",EDGE,"E16.23.7.0"),sQuery(id+"F3.wireOp",EDGE,"E16.29.7.0"),sQuery(id+"F3.wireOp",EDGE,"E16.32.7.0"),sQuery(id+"F3.wireOp",EDGE,"E16.36.7.0"),sQuery(id+"F3.wireOp",EDGE,"E16.40.7.0"),sQuery(id+"F3.wireOp",EDGE,"E16.43.7.0"),sQuery(id+"F3.wireOp",EDGE,"E16.46.7.0"),sQuery(id+"F3.wireOp",EDGE,"E16.50.7.0")])],"isStart":false});
            var Q12;
            Q12=makeQuery(id+"F4.opExtrude","CAP_FACE",FACE,{"disambiguationData":[OSD([sQuery(id+"F3.wireOp",EDGE,"E16.1.6.0"),sQuery(id+"F3.wireOp",EDGE,"E16.5.6.0"),sQuery(id+"F3.wireOp",EDGE,"E16.8.6.0"),sQuery(id+"F3.wireOp",EDGE,"E16.14.6.0"),sQuery(id+"F3.wireOp",EDGE,"E16.18.6.0"),sQuery(id+"F3.wireOp",EDGE,"E16.23.6.0"),sQuery(id+"F3.wireOp",EDGE,"E16.29.6.0"),sQuery(id+"F3.wireOp",EDGE,"E16.32.6.0"),sQuery(id+"F3.wireOp",EDGE,"E16.36.6.0"),sQuery(id+"F3.wireOp",EDGE,"E16.40.6.0"),sQuery(id+"F3.wireOp",EDGE,"E16.43.6.0"),sQuery(id+"F3.wireOp",EDGE,"E16.46.6.0"),sQuery(id+"F3.wireOp",EDGE,"E16.50.6.0")])],"isStart":false});
            var Q13;
            Q13=makeQuery(id+"F4.opExtrude","CAP_FACE",FACE,{"disambiguationData":[OSD([sQuery(id+"F3.wireOp",EDGE,"E16.1.9.0"),sQuery(id+"F3.wireOp",EDGE,"E16.5.9.0"),sQuery(id+"F3.wireOp",EDGE,"E16.8.9.0"),sQuery(id+"F3.wireOp",EDGE,"E16.14.9.0"),sQuery(id+"F3.wireOp",EDGE,"E16.18.9.0"),sQuery(id+"F3.wireOp",EDGE,"E16.23.9.0"),sQuery(id+"F3.wireOp",EDGE,"E16.29.9.0"),sQuery(id+"F3.wireOp",EDGE,"E16.32.9.0"),sQuery(id+"F3.wireOp",EDGE,"E16.36.9.0"),sQuery(id+"F3.wireOp",EDGE,"E16.40.9.0"),sQuery(id+"F3.wireOp",EDGE,"E16.43.9.0"),sQuery(id+"F3.wireOp",EDGE,"E16.46.9.0"),sQuery(id+"F3.wireOp",EDGE,"E16.50.9.0")])],"isStart":false});
            var Q14;
            Q14=makeQuery(id+"F4.opExtrude","CAP_FACE",FACE,{"disambiguationData":[OSD([sQuery(id+"F3.wireOp",EDGE,"E16.1.8.0"),sQuery(id+"F3.wireOp",EDGE,"E16.5.8.0"),sQuery(id+"F3.wireOp",EDGE,"E16.8.8.0"),sQuery(id+"F3.wireOp",EDGE,"E16.14.8.0"),sQuery(id+"F3.wireOp",EDGE,"E16.18.8.0"),sQuery(id+"F3.wireOp",EDGE,"E16.23.8.0"),sQuery(id+"F3.wireOp",EDGE,"E16.29.8.0"),sQuery(id+"F3.wireOp",EDGE,"E16.32.8.0"),sQuery(id+"F3.wireOp",EDGE,"E16.36.8.0"),sQuery(id+"F3.wireOp",EDGE,"E16.40.8.0"),sQuery(id+"F3.wireOp",EDGE,"E16.43.8.0"),sQuery(id+"F3.wireOp",EDGE,"E16.46.8.0"),sQuery(id+"F3.wireOp",EDGE,"E16.50.8.0")])],"isStart":false});
            var Q15;
            Q15=makeQuery(id+"F4.opExtrude","CAP_FACE",FACE,{"disambiguationData":[OSD([sQuery(id+"F3.wireOp",EDGE,"E16.1.10.0"),sQuery(id+"F3.wireOp",EDGE,"E16.5.10.0"),sQuery(id+"F3.wireOp",EDGE,"E16.8.10.0"),sQuery(id+"F3.wireOp",EDGE,"E16.14.10.0"),sQuery(id+"F3.wireOp",EDGE,"E16.18.10.0"),sQuery(id+"F3.wireOp",EDGE,"E16.23.10.0"),sQuery(id+"F3.wireOp",EDGE,"E16.29.10.0"),sQuery(id+"F3.wireOp",EDGE,"E16.32.10.0"),sQuery(id+"F3.wireOp",EDGE,"E16.36.10.0"),sQuery(id+"F3.wireOp",EDGE,"E16.40.10.0"),sQuery(id+"F3.wireOp",EDGE,"E16.43.10.0"),sQuery(id+"F3.wireOp",EDGE,"E16.46.10.0"),sQuery(id+"F3.wireOp",EDGE,"E16.50.10.0")])],"isStart":false});
            var Q16;
            Q16=makeQuery(id+"F4.opExtrude","CAP_FACE",FACE,{"disambiguationData":[OSD([sQuery(id+"F3.wireOp",EDGE,"E16.1.11.0"),sQuery(id+"F3.wireOp",EDGE,"E16.5.11.0"),sQuery(id+"F3.wireOp",EDGE,"E16.8.11.0"),sQuery(id+"F3.wireOp",EDGE,"E16.14.11.0"),sQuery(id+"F3.wireOp",EDGE,"E16.18.11.0"),sQuery(id+"F3.wireOp",EDGE,"E16.23.11.0"),sQuery(id+"F3.wireOp",EDGE,"E16.29.11.0"),sQuery(id+"F3.wireOp",EDGE,"E16.32.11.0"),sQuery(id+"F3.wireOp",EDGE,"E16.36.11.0"),sQuery(id+"F3.wireOp",EDGE,"E16.40.11.0"),sQuery(id+"F3.wireOp",EDGE,"E16.43.11.0"),sQuery(id+"F3.wireOp",EDGE,"E16.46.11.0"),sQuery(id+"F3.wireOp",EDGE,"E16.50.11.0")])],"isStart":false});
            var Q17;
            Q17=makeQuery(id+"F4.opExtrude","CAP_FACE",FACE,{"disambiguationData":[OSD([sQuery(id+"F3.wireOp",EDGE,"E16.1.12.0"),sQuery(id+"F3.wireOp",EDGE,"E16.5.12.0"),sQuery(id+"F3.wireOp",EDGE,"E16.8.12.0"),sQuery(id+"F3.wireOp",EDGE,"E16.14.12.0"),sQuery(id+"F3.wireOp",EDGE,"E16.18.12.0"),sQuery(id+"F3.wireOp",EDGE,"E16.23.12.0"),sQuery(id+"F3.wireOp",EDGE,"E16.29.12.0"),sQuery(id+"F3.wireOp",EDGE,"E16.32.12.0"),sQuery(id+"F3.wireOp",EDGE,"E16.36.12.0"),sQuery(id+"F3.wireOp",EDGE,"E16.40.12.0"),sQuery(id+"F3.wireOp",EDGE,"E16.43.12.0"),sQuery(id+"F3.wireOp",EDGE,"E16.46.12.0"),sQuery(id+"F3.wireOp",EDGE,"E16.50.12.0")])],"isStart":false});
            var Q18;
            Q18=makeQuery(id+"F4.opExtrude","CAP_FACE",FACE,{"disambiguationData":[OSD([sQuery(id+"F3.wireOp",EDGE,"E16.1.15.0"),sQuery(id+"F3.wireOp",EDGE,"E16.5.15.0"),sQuery(id+"F3.wireOp",EDGE,"E16.8.15.0"),sQuery(id+"F3.wireOp",EDGE,"E16.14.15.0"),sQuery(id+"F3.wireOp",EDGE,"E16.18.15.0"),sQuery(id+"F3.wireOp",EDGE,"E16.23.15.0"),sQuery(id+"F3.wireOp",EDGE,"E16.29.15.0"),sQuery(id+"F3.wireOp",EDGE,"E16.32.15.0"),sQuery(id+"F3.wireOp",EDGE,"E16.36.15.0"),sQuery(id+"F3.wireOp",EDGE,"E16.40.15.0"),sQuery(id+"F3.wireOp",EDGE,"E16.43.15.0"),sQuery(id+"F3.wireOp",EDGE,"E16.46.15.0"),sQuery(id+"F3.wireOp",EDGE,"E16.50.15.0")])],"isStart":false});
            var Q19;
            Q19=makeQuery(id+"F4.opExtrude","CAP_FACE",FACE,{"disambiguationData":[OSD([sQuery(id+"F3.wireOp",EDGE,"E16.1.16.0"),sQuery(id+"F3.wireOp",EDGE,"E16.5.16.0"),sQuery(id+"F3.wireOp",EDGE,"E16.8.16.0"),sQuery(id+"F3.wireOp",EDGE,"E16.14.16.0"),sQuery(id+"F3.wireOp",EDGE,"E16.18.16.0"),sQuery(id+"F3.wireOp",EDGE,"E16.23.16.0"),sQuery(id+"F3.wireOp",EDGE,"E16.29.16.0"),sQuery(id+"F3.wireOp",EDGE,"E16.32.16.0"),sQuery(id+"F3.wireOp",EDGE,"E16.36.16.0"),sQuery(id+"F3.wireOp",EDGE,"E16.40.16.0"),sQuery(id+"F3.wireOp",EDGE,"E16.43.16.0"),sQuery(id+"F3.wireOp",EDGE,"E16.46.16.0"),sQuery(id+"F3.wireOp",EDGE,"E16.50.16.0")])],"isStart":false});
            var Q20;
            Q20=makeQuery(id+"F4.opExtrude","CAP_FACE",FACE,{"disambiguationData":[OSD([sQuery(id+"F3.wireOp",EDGE,"E16.1.13.0"),sQuery(id+"F3.wireOp",EDGE,"E16.5.13.0"),sQuery(id+"F3.wireOp",EDGE,"E16.8.13.0"),sQuery(id+"F3.wireOp",EDGE,"E16.14.13.0"),sQuery(id+"F3.wireOp",EDGE,"E16.18.13.0"),sQuery(id+"F3.wireOp",EDGE,"E16.23.13.0"),sQuery(id+"F3.wireOp",EDGE,"E16.29.13.0"),sQuery(id+"F3.wireOp",EDGE,"E16.32.13.0"),sQuery(id+"F3.wireOp",EDGE,"E16.36.13.0"),sQuery(id+"F3.wireOp",EDGE,"E16.40.13.0"),sQuery(id+"F3.wireOp",EDGE,"E16.43.13.0"),sQuery(id+"F3.wireOp",EDGE,"E16.46.13.0"),sQuery(id+"F3.wireOp",EDGE,"E16.50.13.0")])],"isStart":false});
            var Q21;
            Q21=makeQuery(id+"F4.opExtrude","CAP_FACE",FACE,{"disambiguationData":[OSD([sQuery(id+"F3.wireOp",EDGE,"E16.1.14.0"),sQuery(id+"F3.wireOp",EDGE,"E16.5.14.0"),sQuery(id+"F3.wireOp",EDGE,"E16.8.14.0"),sQuery(id+"F3.wireOp",EDGE,"E16.14.14.0"),sQuery(id+"F3.wireOp",EDGE,"E16.18.14.0"),sQuery(id+"F3.wireOp",EDGE,"E16.23.14.0"),sQuery(id+"F3.wireOp",EDGE,"E16.29.14.0"),sQuery(id+"F3.wireOp",EDGE,"E16.32.14.0"),sQuery(id+"F3.wireOp",EDGE,"E16.36.14.0"),sQuery(id+"F3.wireOp",EDGE,"E16.40.14.0"),sQuery(id+"F3.wireOp",EDGE,"E16.43.14.0"),sQuery(id+"F3.wireOp",EDGE,"E16.46.14.0"),sQuery(id+"F3.wireOp",EDGE,"E16.50.14.0")])],"isStart":false});
            var Q22;
            Q22=makeQuery(id+"F4.opExtrude","CAP_FACE",FACE,{"disambiguationData":[OSD([sQuery(id+"F3.wireOp",EDGE,"E16.1.17.0"),sQuery(id+"F3.wireOp",EDGE,"E16.5.17.0"),sQuery(id+"F3.wireOp",EDGE,"E16.8.17.0"),sQuery(id+"F3.wireOp",EDGE,"E16.14.17.0"),sQuery(id+"F3.wireOp",EDGE,"E16.18.17.0"),sQuery(id+"F3.wireOp",EDGE,"E16.23.17.0"),sQuery(id+"F3.wireOp",EDGE,"E16.29.17.0"),sQuery(id+"F3.wireOp",EDGE,"E16.32.17.0"),sQuery(id+"F3.wireOp",EDGE,"E16.36.17.0"),sQuery(id+"F3.wireOp",EDGE,"E16.40.17.0"),sQuery(id+"F3.wireOp",EDGE,"E16.43.17.0"),sQuery(id+"F3.wireOp",EDGE,"E16.46.17.0"),sQuery(id+"F3.wireOp",EDGE,"E16.50.17.0")])],"isStart":false});
            var Q23;
            Q23=makeQuery(id+"F4.opExtrude","CAP_FACE",FACE,{"disambiguationData":[OSD([sQuery(id+"F3.wireOp",EDGE,"E16.1.18.0"),sQuery(id+"F3.wireOp",EDGE,"E16.5.18.0"),sQuery(id+"F3.wireOp",EDGE,"E16.8.18.0"),sQuery(id+"F3.wireOp",EDGE,"E16.14.18.0"),sQuery(id+"F3.wireOp",EDGE,"E16.18.18.0"),sQuery(id+"F3.wireOp",EDGE,"E16.23.18.0"),sQuery(id+"F3.wireOp",EDGE,"E16.29.18.0"),sQuery(id+"F3.wireOp",EDGE,"E16.32.18.0"),sQuery(id+"F3.wireOp",EDGE,"E16.36.18.0"),sQuery(id+"F3.wireOp",EDGE,"E16.40.18.0"),sQuery(id+"F3.wireOp",EDGE,"E16.43.18.0"),sQuery(id+"F3.wireOp",EDGE,"E16.46.18.0"),sQuery(id+"F3.wireOp",EDGE,"E16.50.18.0")])],"isStart":false});
            var Q24;
            Q24=makeQuery(id+"F4.opExtrude","CAP_FACE",FACE,{"disambiguationData":[OSD([sQuery(id+"F3.wireOp",EDGE,"E16.1.24.0"),sQuery(id+"F3.wireOp",EDGE,"E16.5.24.0"),sQuery(id+"F3.wireOp",EDGE,"E16.8.24.0"),sQuery(id+"F3.wireOp",EDGE,"E16.14.24.0"),sQuery(id+"F3.wireOp",EDGE,"E16.18.24.0"),sQuery(id+"F3.wireOp",EDGE,"E16.23.24.0"),sQuery(id+"F3.wireOp",EDGE,"E16.29.24.0"),sQuery(id+"F3.wireOp",EDGE,"E16.32.24.0"),sQuery(id+"F3.wireOp",EDGE,"E16.36.24.0"),sQuery(id+"F3.wireOp",EDGE,"E16.40.24.0"),sQuery(id+"F3.wireOp",EDGE,"E16.43.24.0"),sQuery(id+"F3.wireOp",EDGE,"E16.46.24.0"),sQuery(id+"F3.wireOp",EDGE,"E16.50.24.0")])],"isStart":false});
            var Q25;
            Q25=makeQuery(id+"F4.opExtrude","CAP_FACE",FACE,{"disambiguationData":[OSD([sQuery(id+"F3.wireOp",EDGE,"E16.1.23.0"),sQuery(id+"F3.wireOp",EDGE,"E16.5.23.0"),sQuery(id+"F3.wireOp",EDGE,"E16.8.23.0"),sQuery(id+"F3.wireOp",EDGE,"E16.14.23.0"),sQuery(id+"F3.wireOp",EDGE,"E16.18.23.0"),sQuery(id+"F3.wireOp",EDGE,"E16.23.23.0"),sQuery(id+"F3.wireOp",EDGE,"E16.29.23.0"),sQuery(id+"F3.wireOp",EDGE,"E16.32.23.0"),sQuery(id+"F3.wireOp",EDGE,"E16.36.23.0"),sQuery(id+"F3.wireOp",EDGE,"E16.40.23.0"),sQuery(id+"F3.wireOp",EDGE,"E16.43.23.0"),sQuery(id+"F3.wireOp",EDGE,"E16.46.23.0"),sQuery(id+"F3.wireOp",EDGE,"E16.50.23.0")])],"isStart":false});
            var Q26;
            Q26=makeQuery(id+"F4.opExtrude","CAP_FACE",FACE,{"disambiguationData":[OSD([sQuery(id+"F3.wireOp",EDGE,"E16.1.22.0"),sQuery(id+"F3.wireOp",EDGE,"E16.5.22.0"),sQuery(id+"F3.wireOp",EDGE,"E16.8.22.0"),sQuery(id+"F3.wireOp",EDGE,"E16.14.22.0"),sQuery(id+"F3.wireOp",EDGE,"E16.18.22.0"),sQuery(id+"F3.wireOp",EDGE,"E16.23.22.0"),sQuery(id+"F3.wireOp",EDGE,"E16.29.22.0"),sQuery(id+"F3.wireOp",EDGE,"E16.32.22.0"),sQuery(id+"F3.wireOp",EDGE,"E16.36.22.0"),sQuery(id+"F3.wireOp",EDGE,"E16.40.22.0"),sQuery(id+"F3.wireOp",EDGE,"E16.43.22.0"),sQuery(id+"F3.wireOp",EDGE,"E16.46.22.0"),sQuery(id+"F3.wireOp",EDGE,"E16.50.22.0")])],"isStart":false});
            var Q27;
            Q27=makeQuery(id+"F4.opExtrude","CAP_FACE",FACE,{"disambiguationData":[OSD([sQuery(id+"F3.wireOp",EDGE,"E16.1.21.0"),sQuery(id+"F3.wireOp",EDGE,"E16.5.21.0"),sQuery(id+"F3.wireOp",EDGE,"E16.8.21.0"),sQuery(id+"F3.wireOp",EDGE,"E16.14.21.0"),sQuery(id+"F3.wireOp",EDGE,"E16.18.21.0"),sQuery(id+"F3.wireOp",EDGE,"E16.23.21.0"),sQuery(id+"F3.wireOp",EDGE,"E16.29.21.0"),sQuery(id+"F3.wireOp",EDGE,"E16.32.21.0"),sQuery(id+"F3.wireOp",EDGE,"E16.36.21.0"),sQuery(id+"F3.wireOp",EDGE,"E16.40.21.0"),sQuery(id+"F3.wireOp",EDGE,"E16.43.21.0"),sQuery(id+"F3.wireOp",EDGE,"E16.46.21.0"),sQuery(id+"F3.wireOp",EDGE,"E16.50.21.0")])],"isStart":false});
            var Q28;
            Q28=makeQuery(id+"F4.opExtrude","CAP_FACE",FACE,{"disambiguationData":[OSD([sQuery(id+"F3.wireOp",EDGE,"E16.1.20.0"),sQuery(id+"F3.wireOp",EDGE,"E16.5.20.0"),sQuery(id+"F3.wireOp",EDGE,"E16.8.20.0"),sQuery(id+"F3.wireOp",EDGE,"E16.14.20.0"),sQuery(id+"F3.wireOp",EDGE,"E16.18.20.0"),sQuery(id+"F3.wireOp",EDGE,"E16.23.20.0"),sQuery(id+"F3.wireOp",EDGE,"E16.29.20.0"),sQuery(id+"F3.wireOp",EDGE,"E16.32.20.0"),sQuery(id+"F3.wireOp",EDGE,"E16.36.20.0"),sQuery(id+"F3.wireOp",EDGE,"E16.40.20.0"),sQuery(id+"F3.wireOp",EDGE,"E16.43.20.0"),sQuery(id+"F3.wireOp",EDGE,"E16.46.20.0"),sQuery(id+"F3.wireOp",EDGE,"E16.50.20.0")])],"isStart":false});
            var Q29;
            Q29=makeQuery(id+"F4.opExtrude","CAP_FACE",FACE,{"disambiguationData":[OSD([sQuery(id+"F3.wireOp",EDGE,"E16.1.19.0"),sQuery(id+"F3.wireOp",EDGE,"E16.5.19.0"),sQuery(id+"F3.wireOp",EDGE,"E16.8.19.0"),sQuery(id+"F3.wireOp",EDGE,"E16.14.19.0"),sQuery(id+"F3.wireOp",EDGE,"E16.18.19.0"),sQuery(id+"F3.wireOp",EDGE,"E16.23.19.0"),sQuery(id+"F3.wireOp",EDGE,"E16.29.19.0"),sQuery(id+"F3.wireOp",EDGE,"E16.32.19.0"),sQuery(id+"F3.wireOp",EDGE,"E16.36.19.0"),sQuery(id+"F3.wireOp",EDGE,"E16.40.19.0"),sQuery(id+"F3.wireOp",EDGE,"E16.43.19.0"),sQuery(id+"F3.wireOp",EDGE,"E16.46.19.0"),sQuery(id+"F3.wireOp",EDGE,"E16.50.19.0")])],"isStart":false});
            extrude(context, id + "F5", {"entities" : qUnion([Q0, Q1, Q2, Q3, Q4, Q5, Q6, Q7, Q8, Q9, Q10, Q11, Q12, Q13, Q14, Q15, Q16, Q17, Q18, Q19, Q20, Q21, Q22, Q23, Q24, Q25, Q26, Q27, Q28, Q29]), "operationType" : NewBodyOperationType.ADD, "depth" : 57.15 * mm});
        }
        {
            var Q0;
            Q0=makeQuery(id+"F4.boolean.opBoolean","MERGE",FACE,{"derivedFrom":[makeQuery(id+"F1.opExtrude","CAP_FACE",FACE,{"disambiguationData":[OSD([sQuery(id+"F0.wireOp",EDGE,"E0")])],"isStart":false}),makeQuery(id+"F4.opExtrude","CAP_FACE",FACE,{"disambiguationData":[OSD([sQuery(id+"F3.wireOp",EDGE,"E1.trimOffspring"),sQuery(id+"F3.wireOp",EDGE,"E2"),sQuery(id+"F3.wireOp",EDGE,"E3"),sQuery(id+"F3.wireOp",EDGE,"E4.MirrorCS"),sQuery(id+"F3.wireOp",EDGE,"E5.MirrorCS"),sQuery(id+"F3.wireOp",EDGE,"E7.filletArc"),sQuery(id+"F3.wireOp",EDGE,"E8"),sQuery(id+"F3.wireOp",EDGE,"E9.MirrorCS"),sQuery(id+"F3.wireOp",EDGE,"E10.MirrorCS"),sQuery(id+"F3.wireOp",EDGE,"E11.filletArc"),sQuery(id+"F3.wireOp",EDGE,"E12.filletArc"),sQuery(id+"F3.wireOp",EDGE,"E13.filletArc"),sQuery(id+"F3.wireOp",EDGE,"E14.filletArc")])],"isStart":true})]});
            var sketch = newSketch(context, id + "F6", { "sketchPlane" : qUnion([Q0])});
            skPoint(sketch, "E17", {"position": v(0, 0) * mm});
            skSolve(sketch);
        }
        {
            var Q0;
            {var subQ144=sQuery(id+"F3.wireOp",EDGE,"E1.trimOffspring");Q0=makeQuery(id+"F6.imprint","IMPRINT",FACE,{"disambiguationData":[TD([[makeQuery(id+"F6.imprint","IMPRINT",EDGE,{"derivedFrom":makeQuery(id+"F4.opExtrude","CAP_EDGE",EDGE,{"disambiguationData":[OSD([subQ144])],"isStart":true})}),1.0]])]});}
            var sketch = newSketch(context, id + "F7", { "sketchPlane" : qUnion([Q0])});
            skCircle(sketch, "E18", {"center": v(0, 0) * mm, "radius": 12.7 * mm});
            skSolve(sketch);
        }
        {
            var Q0;
            Q0=qSketchRegion(id+"F7",true);
            extrude(context, id + "F8", {"entities" : qUnion([Q0]), "operationType" : NewBodyOperationType.ADD, "depth" : 12.7 * mm});
        }
        {
            var Q0;
            Q0=makeQuery(id+"F8.opExtrude","CAP_FACE",FACE,{"disambiguationData":[OSD([sQuery(id+"F7.wireOp",EDGE,"E18")])],"isStart":false});
            var sketch = newSketch(context, id + "F9", { "sketchPlane" : qUnion([Q0])});
            skCircle(sketch, "E19", {"center": v(0, 0) * mm, "radius": 6.35 * mm});
            skSolve(sketch);
        }
        {
            var Q0;
            Q0=makeQuery(id+"F9.imprint","IMPRINT",FACE,{"disambiguationData":[TD([[makeQuery(id+"F9.imprint","IMPRINT",EDGE,{"derivedFrom":sQuery(id+"F9.wireOp",EDGE,"E19")}),1.0]])]});
            extrude(context, id + "F10", {"entities" : qUnion([Q0]), "operationType" : NewBodyOperationType.REMOVE, "oppositeDirection" : true, "depth" : 127 * mm});
        }
    });
